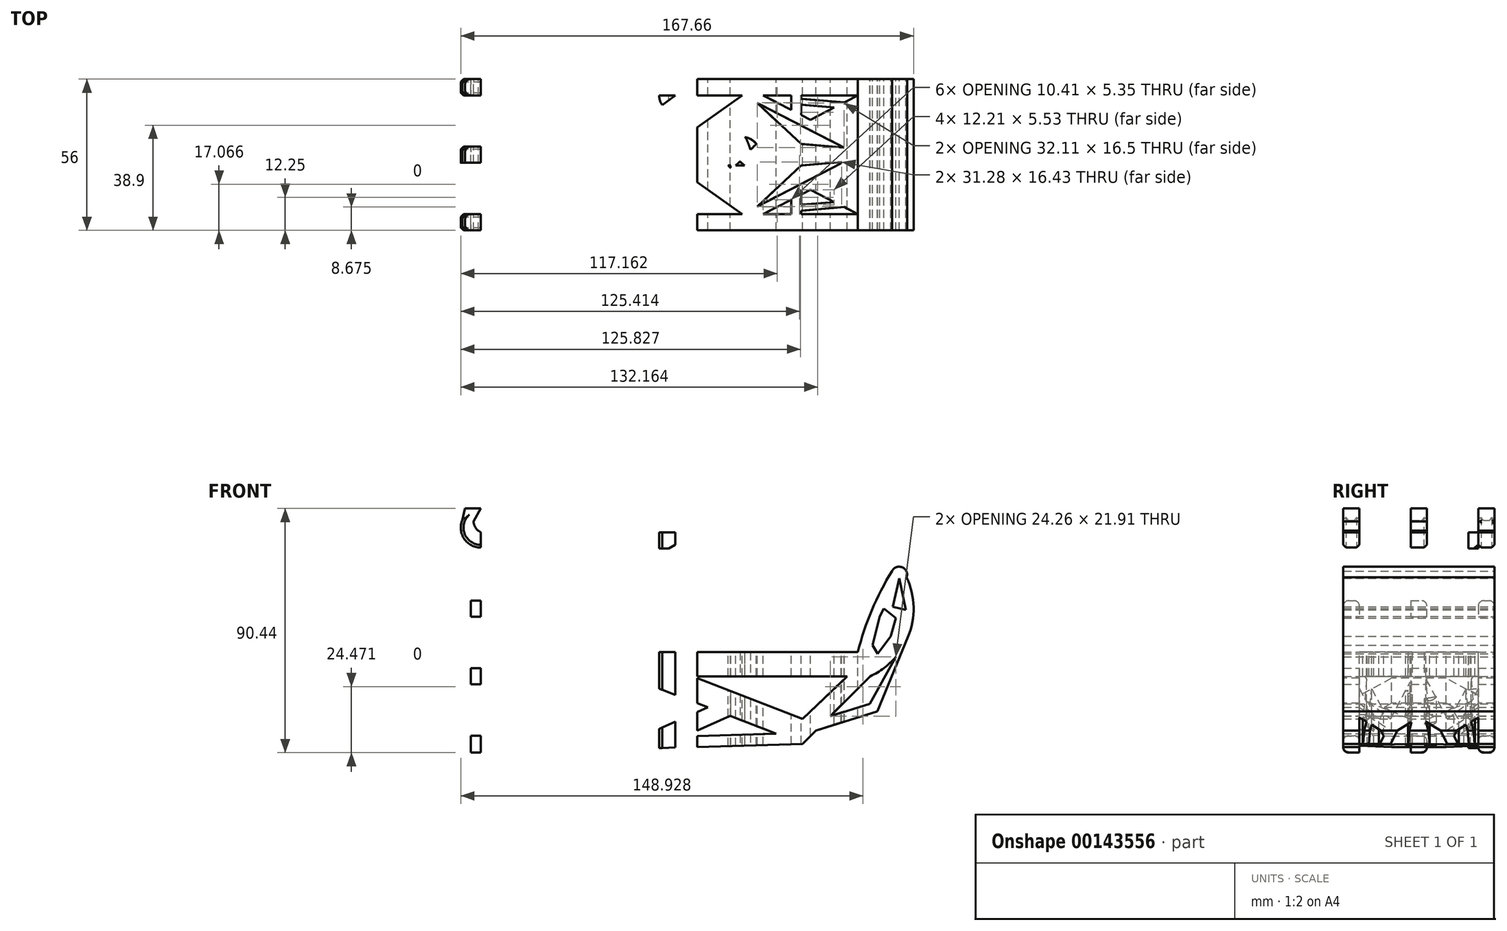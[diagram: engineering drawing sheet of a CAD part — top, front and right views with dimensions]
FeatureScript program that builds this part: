
annotation { "Feature Type Name" : "Feature", "Feature Type Description" : "" }
export const myFeature = defineFeature(function(context is Context, id is Id, definition is map)
    precondition{}
    {
        {
            var Q0;
            Q0=qCreatedBy(makeId("Front.planeOp"),FACE);
            var sketch = newSketch(context, id + "F0", { "sketchPlane" : qUnion([Q0])});
            skLineSegment(sketch, "E0.bottom", {"start": v(0, 0) * mm, "end": v(2.2, 0) * mm});
            skLineSegment(sketch, "E0.top", {"start": v(0, 6) * mm, "end": v(2.2, 6) * mm});
            skLineSegment(sketch, "E0.left", {"start": v(0, 0) * mm, "end": v(0, 6) * mm});
            skLineSegment(sketch, "E1.bottom", {"start": v(0, 6) * mm, "end": v(-4.66, 6) * mm});
            skLineSegment(sketch, "E1.top", {"start": v(0, 0.4) * mm, "end": v(-4.66, 0.4) * mm});
            skLineSegment(sketch, "E1.left", {"start": v(0, 6) * mm, "end": v(0, 0.4) * mm});
            skLineSegment(sketch, "E1.right", {"start": v(-4.66, 6) * mm, "end": v(-4.66, 0.4) * mm});
            skArc(sketch, "E2", {"start": v(-7.33, 10.05) * mm, "mid": v(-6.52, 7.68) * mm, "end": v(-4.66, 6) * mm});
            skArc(sketch, "E3", {"start": v(-11.52, 10.48) * mm, "mid": v(-10.76, 3.63) * mm, "end": v(-4.66, 0.4) * mm});
            skLineSegment(sketch, "E4", {"start": v(-4.66, 14.86) * mm, "end": v(-10.43, 14.86) * mm});
            skLineSegment(sketch, "E5", {"start": v(-10.43, 14.86) * mm, "end": v(-12, 8.6) * mm});
            skLineSegment(sketch, "E6", {"start": v(-4.66, 14.86) * mm, "end": v(-7.33, 10.05) * mm});
            skLineSegment(sketch, "E7", {"start": v(-8.25, 8.4) * mm, "end": v(-4.66, 6) * mm});
            skLineSegment(sketch, "E8.bottom", {"start": v(0, 6) * mm, "end": v(8, 6) * mm});
            skLineSegment(sketch, "E8.left", {"start": v(0, 6) * mm, "end": v(0, -7.26) * mm});
            skLineSegment(sketch, "E8.right", {"start": v(8, 6) * mm, "end": v(8, -7.26) * mm});
            skPoint(sketch, "E9.startSnap0", {"position": v(8, -0.63) * mm});
            skLineSegment(sketch, "E10.left", {"start": v(0, -7.26) * mm, "end": v(0, -22.3) * mm});
            skLineSegment(sketch, "E11", {"start": v(0, 3.2) * mm, "end": v(0, -22.3) * mm, "construction": true});
            skLineSegment(sketch, "E12.bottom", {"start": v(-8.37, -19.3) * mm, "end": v(0, -19.3) * mm});
            skLineSegment(sketch, "E12.top", {"start": v(-8.37, -25.3) * mm, "end": v(8, -25.3) * mm});
            skLineSegment(sketch, "E12.left", {"start": v(-8.37, -19.3) * mm, "end": v(-8.37, -25.3) * mm});
            skPoint(sketch, "E12.middle", {"position": v(0, -22.3) * mm});
            skLineSegment(sketch, "E13", {"start": v(8, -7.26) * mm, "end": v(8, -25.3) * mm});
            skLineSegment(sketch, "E14", {"start": v(0, -25.3) * mm, "end": v(-8.37, -25.3) * mm});
            skPoint(sketch, "E12.right.start.orphan", {"position": v(8.37, -19.3) * mm});
            skPoint(sketch, "E15.orphan", {"position": v(8.37, -25.3) * mm});
            skPoint(sketch, "E9.start.orphan", {"position": v(8, 0) * mm});
            skPoint(sketch, "E16.start.orphan", {"position": v(37.05, 0) * mm});
            skLineSegment(sketch, "E17.top", {"start": v(0, -47.3) * mm, "end": v(0.27, -47.3) * mm});
            skLineSegment(sketch, "E17.left", {"start": v(0, -22.3) * mm, "end": v(0, -38.12) * mm});
            skLineSegment(sketch, "E17.right", {"start": v(8, -22.3) * mm, "end": v(8, -38.33) * mm});
            skLineSegment(sketch, "E18.bottom", {"start": v(-8.37, -44.3) * mm, "end": v(0.18, -44.3) * mm});
            skLineSegment(sketch, "E18.top", {"start": v(-8.37, -50.3) * mm, "end": v(0.36, -50.3) * mm});
            skLineSegment(sketch, "E18.left", {"start": v(-8.37, -44.3) * mm, "end": v(-8.37, -50.3) * mm});
            skLineSegment(sketch, "E18.right", {"start": v(8.37, -47.3) * mm, "end": v(8.37, -47.46) * mm});
            skPoint(sketch, "E18.middle", {"position": v(0, -47.3) * mm});
            skLineSegment(sketch, "E19.bottom", {"start": v(8.37, -44.3) * mm, "end": v(8, -44.3) * mm});
            skLineSegment(sketch, "E19.top", {"start": v(0.36, -50.3) * mm, "end": v(-8.37, -50.3) * mm});
            skPoint(sketch, "E19.middle", {"position": v(8, -47.3) * mm});
            skPoint(sketch, "E19.right.end.orphan", {"position": v(-128, -50.3) * mm});
            skPoint(sketch, "E19.right.start.orphan", {"position": v(-119, -44.3) * mm});
            skLineSegment(sketch, "E20.bottom", {"start": v(0, 6) * mm, "end": v(75.48, 6) * mm});
            skLineSegment(sketch, "E20.left", {"start": v(0, 6) * mm, "end": v(0, 0) * mm});
            skLineSegment(sketch, "E21.bottom", {"start": v(8, -38.33) * mm, "end": v(133.63, -38.33) * mm});
            skLineSegment(sketch, "E21.left", {"start": v(8, -36.1) * mm, "end": v(8, -38.33) * mm});
            skLineSegment(sketch, "E22.bottom", {"start": v(8, -38.33) * mm, "end": v(135, -38.33) * mm});
            skLineSegment(sketch, "E22.top", {"start": v(8, -47.3) * mm, "end": v(8.37, -47.3) * mm});
            skPoint(sketch, "E23.endSnap0", {"position": v(4, -47.3) * mm});
            skLineSegment(sketch, "E24", {"start": v(4, -47.3) * mm, "end": v(4, -50.3) * mm});
            skLineSegment(sketch, "E25", {"start": v(139.5, -47.3) * mm, "end": v(114.54, -72.3) * mm});
            skLineSegment(sketch, "E26", {"start": v(104.76, -68.54) * mm, "end": v(87.68, -61.97) * mm});
            skLineSegment(sketch, "E27", {"start": v(131.03, -47.3) * mm, "end": v(114.54, -63.04) * mm});
            skLineSegment(sketch, "E28", {"start": v(114.54, -63.04) * mm, "end": v(73.6, -47.3) * mm});
            skPoint(sketch, "E29.centerSnap0", {"position": v(4, -59.8) * mm});
            skLineSegment(sketch, "E30", {"start": v(17.34, -47.3) * mm, "end": v(10.24, -53.9) * mm});
            skLineSegment(sketch, "E31", {"start": v(10.24, -53.9) * mm, "end": v(10.24, -64.47) * mm});
            skLineSegment(sketch, "E32", {"start": v(10.24, -64.47) * mm, "end": v(15, -66.9) * mm});
            skLineSegment(sketch, "E33", {"start": v(15, -66.9) * mm, "end": v(27.64, -60.68) * mm});
            skLineSegment(sketch, "E34.bottom", {"start": v(-4.5, -69.3) * mm, "end": v(4, -69.3) * mm});
            skLineSegment(sketch, "E34.top", {"start": v(-4.5, -75.3) * mm, "end": v(12.5, -75.3) * mm});
            skPoint(sketch, "E34.middle", {"position": v(4, -72.3) * mm});
            skLineSegment(sketch, "E35", {"start": v(21.25, -71) * mm, "end": v(36.6, -63.46) * mm});
            skLineSegment(sketch, "E36", {"start": v(12.5, -75.3) * mm, "end": v(114.54, -72.3) * mm});
            skPoint(sketch, "E37.end.orphan", {"position": v(4, -77.18) * mm});
            skLineSegment(sketch, "E38", {"start": v(21.25, -71) * mm, "end": v(52.02, -70.1) * mm});
            skPoint(sketch, "E39.orphan", {"position": v(135, -50.3) * mm});
            skPoint(sketch, "E19.left.start.orphan", {"position": v(144, -44.3) * mm});
            skLineSegment(sketch, "E40.trimOffspring", {"start": v(73.6, -47.3) * mm, "end": v(131.03, -47.3) * mm});
            skLineSegment(sketch, "E41", {"start": v(51.94, -55.92) * mm, "end": v(60.4, -51.48) * mm});
            skLineSegment(sketch, "E42", {"start": v(52.53, -48.45) * mm, "end": v(21.76, -47.45) * mm});
            skLineSegment(sketch, "E43", {"start": v(8.37, -47.46) * mm, "end": v(8, -47.3) * mm});
            skLineSegment(sketch, "E44", {"start": v(36.6, -63.46) * mm, "end": v(52.02, -70.1) * mm});
            skLineSegment(sketch, "E45", {"start": v(70.6, -69.54) * mm, "end": v(87.68, -61.97) * mm});
            skLineSegment(sketch, "E46", {"start": v(79.42, -58.8) * mm, "end": v(60.4, -67.23) * mm});
            skLineSegment(sketch, "E47", {"start": v(60.4, -67.23) * mm, "end": v(43.62, -60) * mm});
            skLineSegment(sketch, "E48.trimOffspring", {"start": v(43.62, -60) * mm, "end": v(51.94, -55.92) * mm});
            skPoint(sketch, "E49.end.orphan", {"position": v(60.4, -69.84) * mm});
            skPoint(sketch, "E49.start.orphan", {"position": v(82.58, -60.01) * mm});
            skLineSegment(sketch, "E50.trimOffspring", {"start": v(70.6, -69.54) * mm, "end": v(104.76, -68.54) * mm});
            skPoint(sketch, "E29.center.orphan", {"position": v(17.34, -59.8) * mm});
            skPoint(sketch, "E51.start.orphan", {"position": v(13.8, -50.6) * mm});
            skLineSegment(sketch, "E52", {"start": v(17.34, -47.3) * mm, "end": v(27.64, -60.68) * mm});
            skLineSegment(sketch, "E53", {"start": v(36.48, -56.34) * mm, "end": v(40.82, -54.2) * mm});
            skLineSegment(sketch, "E54", {"start": v(21.76, -47.45) * mm, "end": v(36.48, -56.34) * mm});
            skLineSegment(sketch, "E55.trimOffspring", {"start": v(36.48, -56.34) * mm, "end": v(52.53, -48.45) * mm});
            skArc(sketch, "E56", {"start": v(147.62, -8.33) * mm, "mid": v(140.11, -22.82) * mm, "end": v(135, -38.33) * mm});
            skArc(sketch, "E57", {"start": v(139.5, -47.3) * mm, "mid": v(144.65, -44.25) * mm, "end": v(149.02, -40.15) * mm});
            skArc(sketch, "E58", {"start": v(153.03, -10.64) * mm, "mid": v(151.41, -6.95) * mm, "end": v(147.62, -8.33) * mm});
            skLineSegment(sketch, "E59", {"start": v(150.25, -11.01) * mm, "end": v(152.71, -22.66) * mm});
            skLineSegment(sketch, "E60", {"start": v(147.92, -21.6) * mm, "end": v(152.71, -22.66) * mm});
            skLineSegment(sketch, "E61.trimOffspring", {"start": v(147.92, -21.6) * mm, "end": v(150.25, -11.01) * mm});
            skLineSegment(sketch, "E62", {"start": v(149.02, -40.15) * mm, "end": v(139.32, -57.51) * mm});
            skLineSegment(sketch, "E63", {"start": v(139.32, -57.51) * mm, "end": v(124.76, -62.06) * mm});
            skLineSegment(sketch, "E64", {"start": v(124.76, -62.06) * mm, "end": v(119.44, -67.4) * mm});
            skLineSegment(sketch, "E65", {"start": v(119.44, -67.4) * mm, "end": v(142.16, -60.29) * mm});
            skLineSegment(sketch, "E66", {"start": v(142.16, -60.29) * mm, "end": v(153.54, -32.79) * mm});
            skArc(sketch, "E67.trimOffspring", {"start": v(153.54, -32.79) * mm, "mid": v(155.61, -21.66) * mm, "end": v(153.03, -10.64) * mm});
            skLineSegment(sketch, "E68", {"start": v(143.06, -25.11) * mm, "end": v(140.34, -35.8) * mm});
            skLineSegment(sketch, "E69", {"start": v(140.34, -35.8) * mm, "end": v(142.29, -38.91) * mm});
            skLineSegment(sketch, "E70", {"start": v(142.29, -38.91) * mm, "end": v(147.14, -32.5) * mm});
            skLineSegment(sketch, "E71", {"start": v(147.14, -32.5) * mm, "end": v(149.09, -25.7) * mm});
            skLineSegment(sketch, "E72", {"start": v(149.09, -25.7) * mm, "end": v(144.62, -22.2) * mm});
            skLineSegment(sketch, "E73", {"start": v(144.62, -22.2) * mm, "end": v(143.06, -25.11) * mm});
            skPoint(sketch, "E20.right.end.orphan", {"position": v(129.94, 0) * mm});
            skLineSegment(sketch, "E74.trimOffspring", {"start": v(79.42, -58.8) * mm, "end": v(60.4, -51.48) * mm});
            skPoint(sketch, "E34.right.start.orphan", {"position": v(12.5, -69.3) * mm});
            skLineSegment(sketch, "E75", {"start": v(0, -38.12) * mm, "end": v(0.18, -44.3) * mm});
            skLineSegment(sketch, "E76", {"start": v(1.1, -75.3) * mm, "end": v(-8.37, -75.58) * mm});
            skLineSegment(sketch, "E77", {"start": v(-8.37, -75.58) * mm, "end": v(-8.37, -69.3) * mm});
            skLineSegment(sketch, "E78", {"start": v(-8.37, -69.3) * mm, "end": v(-4.5, -69.3) * mm});
            skPoint(sketch, "E79.trimOffspring.start.orphan", {"position": v(-4.5, -72.3) * mm});
            skLineSegment(sketch, "E80.trimOffspring", {"start": v(4, -69.3) * mm, "end": v(4, -72.3) * mm});
            skLineSegment(sketch, "E81.trimOffspring", {"start": v(0.18, -44.3) * mm, "end": v(-8.37, -44.3) * mm});
            skPoint(sketch, "E82.orphan", {"position": v(8.37, -50.3) * mm});
            skLineSegment(sketch, "E83.trimOffspring", {"start": v(0.36, -50.3) * mm, "end": v(0.92, -69.3) * mm});
            skLineSegment(sketch, "E84.trimOffspring", {"start": v(8, 0) * mm, "end": v(64.97, 0) * mm});
            skPoint(sketch, "E85.orphan", {"position": v(8, -19.3) * mm});
            skLineSegment(sketch, "E86", {"start": v(75.48, 6) * mm, "end": v(64.97, 0) * mm});
            skSolve(sketch);
        }
        {
            var Q0;
            Q0=qSketchRegion(id+"F0",true);
            extrude(context, id + "F1", {"entities" : qUnion([Q0]), "depth" : 5.5 * mm});
        }
        {
            var Q0;
            Q0=makeQuery(id+"F1.opExtrude","CAP_EDGE",EDGE,{"disambiguationData":[OSD([sQuery(id+"F0.wireOp",EDGE,"E12.bottom")])],"isStart":false});
            var Q1;
            Q1=makeQuery(id+"F1.opExtrude","CAP_EDGE",EDGE,{"disambiguationData":[OSD([sQuery(id+"F0.wireOp",EDGE,"E12.bottom")])],"isStart":true});
            var Q2;
            Q2=makeQuery(id+"F1.opExtrude","CAP_EDGE",EDGE,{"disambiguationData":[OSD([sQuery(id+"F0.wireOp",EDGE,"E14")])],"isStart":true});
            var Q3;
            Q3=makeQuery(id+"F1.opExtrude","CAP_EDGE",EDGE,{"disambiguationData":[OSD([sQuery(id+"F0.wireOp",EDGE,"E14")])],"isStart":false});
            fillet(context, id + "F2", {"entities" : qUnion([Q0, Q1, Q2, Q3]), "radius" : 2.66 * mm, "tangentPropagation" : true, "allowEdgeOverflow" : false});
        }
        {
            var Q0;
            Q0=makeQuery(id+"F1.opExtrude","SWEPT_EDGE",EDGE,{"disambiguationData":[OSD([sQuery(id+"F0.wireOp",EDGE,"E2"),sQuery(id+"F0.wireOp",EDGE,"E4"),sQuery(id+"F0.wireOp",EDGE,"E6")])]});
            fillet(context, id + "F3", {"entities" : qUnion([Q0]), "radius" : 1.62 * mm, "tangentPropagation" : true, "allowEdgeOverflow" : false});
        }
        {
            var Q0;
            Q0=makeQuery(id+"F1.opExtrude","CAP_EDGE",EDGE,{"disambiguationData":[OSD([sQuery(id+"F0.wireOp",EDGE,"E2")])],"isStart":true});
            var Q1;
            Q1=makeQuery(id+"F1.opExtrude","CAP_EDGE",EDGE,{"disambiguationData":[OSD([sQuery(id+"F0.wireOp",EDGE,"E2")])],"isStart":false});
            var Q2;
            Q2=makeQuery(id+"F1.opExtrude","CAP_EDGE",EDGE,{"disambiguationData":[OSD([sQuery(id+"F0.wireOp",EDGE,"E6")])],"isStart":false});
            var Q3;
            Q3=makeQuery(id+"F1.opExtrude","CAP_EDGE",EDGE,{"disambiguationData":[OSD([sQuery(id+"F0.wireOp",EDGE,"E6")])],"isStart":true});
            fillet(context, id + "F4", {"entities" : qUnion([Q0, Q1, Q2, Q3]), "radius" : .6 * mm, "tangentPropagation" : true, "allowEdgeOverflow" : false});
        }
        {
            var Q0;
            Q0=makeQuery(id+"F1.opExtrude","CAP_EDGE",EDGE,{"disambiguationData":[OSD([sQuery(id+"F0.wireOp",EDGE,"E3")])],"isStart":true});
            var Q1;
            Q1=makeQuery(id+"F1.opExtrude","CAP_EDGE",EDGE,{"disambiguationData":[OSD([sQuery(id+"F0.wireOp",EDGE,"E5")])],"isStart":true});
            var Q2;
            Q2=makeQuery(id+"F1.opExtrude","CAP_EDGE",EDGE,{"disambiguationData":[OSD([sQuery(id+"F0.wireOp",EDGE,"E1.top")])],"isStart":false});
            var Q3;
            Q3=makeQuery(id+"F1.opExtrude","CAP_EDGE",EDGE,{"disambiguationData":[OSD([sQuery(id+"F0.wireOp",EDGE,"E3")])],"isStart":false});
            var Q4;
            Q4=makeQuery(id+"F1.opExtrude","CAP_EDGE",EDGE,{"disambiguationData":[OSD([sQuery(id+"F0.wireOp",EDGE,"E5")])],"isStart":false});
            var Q5;
            Q5=makeQuery(id+"F1.opExtrude","CAP_EDGE",EDGE,{"disambiguationData":[OSD([sQuery(id+"F0.wireOp",EDGE,"E1.top")])],"isStart":true});
            fillet(context, id + "F5", {"entities" : qUnion([Q0, Q1, Q2, Q3, Q4, Q5]), "radius" : 1.49 * mm, "tangentPropagation" : true, "allowEdgeOverflow" : false});
        }
        {
            var Q0;
            Q0=qSketchRegion(id+"F0",true);
            extrude(context, id + "F6", {"entities" : qUnion([Q0]), "operationType" : NewBodyOperationType.ADD, "depth" : 56 * mm});
        }
        {
            var Q0;
            {var subQ0=sQuery(id+"F0.wireOp",EDGE,"E76");Q0=makeQuery(id+"F6.boolean.opBoolean","MERGE",FACE,{"derivedFrom":[makeQuery(id+"F1.opExtrude","SWEPT_FACE",FACE,{"disambiguationData":[OSD([subQ0])]}),makeQuery(id+"F6.opExtrude","SWEPT_FACE",FACE,{"disambiguationData":[OSD([subQ0])]})]});}
            var sketch = newSketch(context, id + "F7", { "sketchPlane" : qUnion([Q0])});
            skLineSegment(sketch, "E87.bottom", {"start": v(-1.12, 56) * mm, "end": v(-15.4, 56) * mm});
            skLineSegment(sketch, "E87.top", {"start": v(-1.12, 0) * mm, "end": v(-15.4, 0) * mm});
            skLineSegment(sketch, "E87.left", {"start": v(-1.12, 56) * mm, "end": v(-1.12, 0) * mm});
            skLineSegment(sketch, "E87.right", {"start": v(-15.4, 56) * mm, "end": v(-15.4, 0) * mm});
            skLineSegment(sketch, "E88.top", {"start": v(-1.12, 50) * mm, "end": v(-15.4, 50) * mm});
            skLineSegment(sketch, "E88.right", {"start": v(-15.4, 56) * mm, "end": v(-15.4, 50) * mm});
            skLineSegment(sketch, "E89.top", {"start": v(-1.12, 6) * mm, "end": v(-15.4, 6) * mm});
            skLineSegment(sketch, "E89.right", {"start": v(-15.4, 0) * mm, "end": v(-15.4, 6) * mm});
            skLineSegment(sketch, "E90.top", {"start": v(-1.12, 31) * mm, "end": v(-15.4, 31) * mm});
            skLineSegment(sketch, "E90.left", {"start": v(-1.12, 28) * mm, "end": v(-1.12, 31) * mm});
            skLineSegment(sketch, "E90.right", {"start": v(-15.4, 28) * mm, "end": v(-15.4, 31) * mm});
            skLineSegment(sketch, "E91.bottom", {"start": v(-15.4, 31) * mm, "end": v(-1.12, 31) * mm});
            skLineSegment(sketch, "E91.top", {"start": v(-15.4, 25) * mm, "end": v(-1.12, 25) * mm});
            skLineSegment(sketch, "E91.left", {"start": v(-15.4, 31) * mm, "end": v(-15.4, 25) * mm});
            skSolve(sketch);
        }
        {
            var Q0;
            {var subQ0=sQuery(id+"F7.wireOp",EDGE,"E88.top");var subQ1=sQuery(id+"F7.wireOp",EDGE,"E87.left");var subQ2=makeQuery(id+"F7.imprint","INTERSECT",VERTEX,{"derivedFrom":[subQ1,subQ0]});Q0=makeQuery(id+"F7.imprint","IMPRINT",FACE,{"disambiguationData":[TD([[makeQuery(id+"F7.imprint","IMPRINT",EDGE,{"disambiguationData":[TD([[subQ2,-1.0]])],"derivedFrom":subQ1}),-1.0]])]});}
            var Q1;
            {var subQ0=sQuery(id+"F7.wireOp",EDGE,"E88.top");var subQ1=sQuery(id+"F7.wireOp",EDGE,"E87.right");var subQ2=makeQuery(id+"F7.imprint","INTERSECT",VERTEX,{"derivedFrom":[subQ1,subQ0,sQuery(id+"F7.wireOp",EDGE,"E88.right")]});Q1=makeQuery(id+"F7.imprint","IMPRINT",FACE,{"disambiguationData":[TD([[makeQuery(id+"F7.imprint","IMPRINT",EDGE,{"disambiguationData":[TD([[subQ2,-1.0]])],"derivedFrom":subQ1}),1.0]])]});}
            var Q2;
            {var subQ0=sQuery(id+"F7.wireOp",EDGE,"E89.top");var subQ1=sQuery(id+"F7.wireOp",EDGE,"E87.left");var subQ2=makeQuery(id+"F7.imprint","INTERSECT",VERTEX,{"derivedFrom":[subQ1,subQ0]});Q2=makeQuery(id+"F7.imprint","IMPRINT",FACE,{"disambiguationData":[TD([[makeQuery(id+"F7.imprint","IMPRINT",EDGE,{"disambiguationData":[TD([[subQ2,1.0]])],"derivedFrom":subQ1}),-1.0]])]});}
            var Q3;
            {var subQ0=sQuery(id+"F7.wireOp",EDGE,"E89.top");var subQ1=sQuery(id+"F7.wireOp",EDGE,"E87.right");var subQ2=makeQuery(id+"F7.imprint","INTERSECT",VERTEX,{"derivedFrom":[subQ1,subQ0,sQuery(id+"F7.wireOp",EDGE,"E89.right")]});Q3=makeQuery(id+"F7.imprint","IMPRINT",FACE,{"disambiguationData":[TD([[makeQuery(id+"F7.imprint","IMPRINT",EDGE,{"disambiguationData":[TD([[subQ2,1.0]])],"derivedFrom":subQ1}),1.0]])]});}
            extrude(context, id + "F8", {"entities" : qUnion([Q0, Q1, Q2, Q3]), "operationType" : NewBodyOperationType.REMOVE, "endBound" : BoundingType.THROUGH_ALL, "oppositeDirection" : true, "depth" : 25 * mm});
        }
        {
            var Q0;
            {var subQ0=sQuery(id+"F0.wireOp",EDGE,"E20.bottom");var subQ1=sQuery(id+"F0.wireOp",EDGE,"E1.bottom");Q0=makeQuery(id+"F6.boolean.opBoolean","MERGE",FACE,{"derivedFrom":[makeQuery(id+"F1.opExtrude","SWEPT_FACE",FACE,{"disambiguationData":[OSD([subQ1,subQ0])]}),makeQuery(id+"F6.opExtrude","SWEPT_FACE",FACE,{"disambiguationData":[OSD([subQ1,subQ0])]})]});}
            var sketch = newSketch(context, id + "F9", { "sketchPlane" : qUnion([Q0])});
            skLineSegment(sketch, "E92.top", {"start": v(15.03, -50) * mm, "end": v(39.96, -50) * mm});
            skLineSegment(sketch, "E93", {"start": v(12.55, -9.31) * mm, "end": v(7.82, -15.65) * mm});
            skLineSegment(sketch, "E94", {"start": v(7.82, -15.65) * mm, "end": v(15.03, -24.07) * mm});
            skPoint(sketch, "E94.endSnap0", {"position": v(7.82, -28) * mm});
            skLineSegment(sketch, "E95", {"start": v(15.03, -31.97) * mm, "end": v(7.82, -40.5) * mm});
            skPoint(sketch, "E95.endSnap0", {"position": v(-1.3, -40.5) * mm});
            skLineSegment(sketch, "E96", {"start": v(7.82, -40.5) * mm, "end": v(12.53, -46.7) * mm});
            skPoint(sketch, "E97.orphan", {"position": v(7.82, -6) * mm});
            skPoint(sketch, "E98.orphan", {"position": v(7.82, -50) * mm});
            skLineSegment(sketch, "E99", {"start": v(15.03, -6) * mm, "end": v(40.59, -6) * mm});
            skLineSegment(sketch, "E100", {"start": v(69.45, -6) * mm, "end": v(66.07, -12.15) * mm});
            skPoint(sketch, "E100.endSnap0", {"position": v(15.03, -15.04) * mm});
            skLineSegment(sketch, "E101", {"start": v(64.61, -15.53) * mm, "end": v(66.79, -24.07) * mm});
            skLineSegment(sketch, "E102", {"start": v(66.74, -31.97) * mm, "end": v(64.49, -40.5) * mm});
            skLineSegment(sketch, "E103", {"start": v(40.86, -6.91) * mm, "end": v(27.3, -15.92) * mm});
            skLineSegment(sketch, "E104", {"start": v(43.56, -6.98) * mm, "end": v(54.86, -15.3) * mm});
            skLineSegment(sketch, "E105", {"start": v(40.21, -49.18) * mm, "end": v(27.11, -40.23) * mm});
            skLineSegment(sketch, "E106", {"start": v(42.59, -49.16) * mm, "end": v(54.67, -40.56) * mm});
            skPoint(sketch, "E92.right.start.orphan", {"position": v(67.79, -6) * mm});
            skLineSegment(sketch, "E107", {"start": v(69.45, -50) * mm, "end": v(66.22, -43.81) * mm});
            skLineSegment(sketch, "E108", {"start": v(18.38, -28) * mm, "end": v(28.6, -21.22) * mm});
            skLineSegment(sketch, "E109", {"start": v(42.24, -12.16) * mm, "end": v(50.7, -18.38) * mm});
            skLineSegment(sketch, "E110", {"start": v(63.76, -28) * mm, "end": v(52.31, -36.15) * mm});
            skLineSegment(sketch, "E111", {"start": v(41.4, -43.9) * mm, "end": v(31.25, -36.89) * mm});
            skLineSegment(sketch, "E112", {"start": v(15.03, -6) * mm, "end": v(27.3, -15.92) * mm});
            skLineSegment(sketch, "E113", {"start": v(69.45, -6) * mm, "end": v(63.55, -10.77) * mm});
            skLineSegment(sketch, "E114.right", {"start": v(45.24, -25) * mm, "end": v(45.24, -25.57) * mm});
            skPoint(sketch, "E114.middle", {"position": v(42.24, -28) * mm});
            skLineSegment(sketch, "E115.trimOffspring", {"start": v(31.48, -19.3) * mm, "end": v(38.63, -25.09) * mm});
            skLineSegment(sketch, "E116.trimOffspring", {"start": v(52.5, -19.7) * mm, "end": v(43.24, -27.2) * mm});
            skLineSegment(sketch, "E117", {"start": v(12.55, -9.31) * mm, "end": v(24.22, -17.97) * mm});
            skLineSegment(sketch, "E118", {"start": v(75.48, -56) * mm, "end": v(0, -56) * mm});
            skLineSegment(sketch, "E119", {"start": v(12.53, -46.7) * mm, "end": v(24.06, -38.15) * mm});
            skLineSegment(sketch, "E120.trimOffspring", {"start": v(28.6, -21.22) * mm, "end": v(36.9, -27.37) * mm});
            skLineSegment(sketch, "E121.trimOffspring", {"start": v(28.4, -34.92) * mm, "end": v(36.9, -28.63) * mm});
            skLineSegment(sketch, "E122", {"start": v(15.03, -50) * mm, "end": v(27.11, -40.23) * mm});
            skLineSegment(sketch, "E123.trimOffspring", {"start": v(45.24, -30.43) * mm, "end": v(52.31, -36.15) * mm});
            skLineSegment(sketch, "E124.trimOffspring", {"start": v(41.61, -25.13) * mm, "end": v(50.7, -18.38) * mm});
            skLineSegment(sketch, "E125.trimOffspring", {"start": v(41.61, -30.87) * mm, "end": v(50.48, -37.45) * mm});
            skPoint(sketch, "E126.orphan", {"position": v(39.24, -28) * mm});
            skLineSegment(sketch, "E127.trimOffspring", {"start": v(43.24, -28.8) * mm, "end": v(52.31, -36.15) * mm});
            skLineSegment(sketch, "E128.trimOffspring", {"start": v(43.24, -27.2) * mm, "end": v(52.5, -19.7) * mm});
            skLineSegment(sketch, "E129.trimOffspring", {"start": v(52.5, -19.7) * mm, "end": v(63.76, -28) * mm});
            skLineSegment(sketch, "E130.trimOffspring", {"start": v(56.48, -16.48) * mm, "end": v(66.79, -24.07) * mm});
            skLineSegment(sketch, "E131.trimOffspring", {"start": v(56.32, -39.39) * mm, "end": v(60.64, -42.88) * mm});
            skLineSegment(sketch, "E132.trimOffspring", {"start": v(54.67, -40.56) * mm, "end": v(59.55, -44.18) * mm});
            skLineSegment(sketch, "E133.trimOffspring", {"start": v(31.25, -36.89) * mm, "end": v(38.63, -30.91) * mm});
            skLineSegment(sketch, "E134.trimOffspring", {"start": v(31.48, -19.3) * mm, "end": v(39.24, -25.57) * mm});
            skPoint(sketch, "E135.end.orphan", {"position": v(45.24, -28) * mm});
            skLineSegment(sketch, "E136.trimOffspring", {"start": v(45.24, -30.43) * mm, "end": v(45.24, -31) * mm});
            skLineSegment(sketch, "E137.trimOffspring", {"start": v(56.32, -39.39) * mm, "end": v(66.74, -31.97) * mm});
            skLineSegment(sketch, "E138.trimOffspring", {"start": v(50.48, -37.45) * mm, "end": v(41.4, -43.9) * mm});
            skLineSegment(sketch, "E139.trimOffspring", {"start": v(31.48, -19.3) * mm, "end": v(42.24, -12.16) * mm});
            skLineSegment(sketch, "E140.trimOffspring", {"start": v(24.22, -17.97) * mm, "end": v(15.03, -24.07) * mm});
            skLineSegment(sketch, "E141.trimOffspring", {"start": v(54.86, -15.3) * mm, "end": v(59.55, -11.82) * mm});
            skLineSegment(sketch, "E142.trimOffspring", {"start": v(56.48, -16.48) * mm, "end": v(60.64, -13.12) * mm});
            skPoint(sketch, "E143.orphan", {"position": v(67.79, -50) * mm});
            skPoint(sketch, "E144.orphan", {"position": v(67.79, -28) * mm});
            skArc(sketch, "E145", {"start": v(42.86, -50) * mm, "mid": v(42.79, -49.56) * mm, "end": v(42.59, -49.16) * mm});
            skArc(sketch, "E146", {"start": v(40.59, -6) * mm, "mid": v(40.66, -6.48) * mm, "end": v(40.86, -6.91) * mm});
            skPoint(sketch, "E147.trimOffspring.end.orphan", {"position": v(39.24, -31) * mm});
            skLineSegment(sketch, "E148.trimOffspring", {"start": v(38.63, -30.91) * mm, "end": v(31.25, -36.89) * mm});
            skArc(sketch, "E149", {"start": v(36.9, -27.37) * mm, "mid": v(36.83, -28) * mm, "end": v(36.9, -28.63) * mm});
            skLineSegment(sketch, "E150.trimOffspring", {"start": v(43.89, -6) * mm, "end": v(57.7, -6) * mm});
            skArc(sketch, "E151.trimOffspring", {"start": v(43.56, -6.98) * mm, "mid": v(43.8, -6.51) * mm, "end": v(43.89, -6) * mm});
            skArc(sketch, "E152.trimOffspring", {"start": v(40.21, -49.18) * mm, "mid": v(40.03, -49.57) * mm, "end": v(39.96, -50) * mm});
            skLineSegment(sketch, "E153.trimOffspring", {"start": v(42.86, -50) * mm, "end": v(67.4, -50) * mm});
            skArc(sketch, "E154.trimOffspring", {"start": v(38.63, -30.91) * mm, "mid": v(40.13, -31.25) * mm, "end": v(41.61, -30.87) * mm});
            skArc(sketch, "E155.trimOffspring", {"start": v(43.24, -28.8) * mm, "mid": v(43.34, -28) * mm, "end": v(43.24, -27.2) * mm});
            skPoint(sketch, "E156.orphan", {"position": v(40.08, -29.74) * mm});
            skArc(sketch, "E157.trimOffspring", {"start": v(41.61, -25.13) * mm, "mid": v(40.13, -24.75) * mm, "end": v(38.63, -25.09) * mm});
            skPoint(sketch, "E114.left.start.orphan", {"position": v(39.24, -25) * mm});
            skArc(sketch, "E158", {"start": v(64.5, -40.47) * mm, "mid": v(62.43, -41.45) * mm, "end": v(60.64, -42.88) * mm});
            skArc(sketch, "E159", {"start": v(66.22, -43.81) * mm, "mid": v(64.8, -44.36) * mm, "end": v(63.55, -45.23) * mm});
            skLineSegment(sketch, "E160", {"start": v(40.08, -28) * mm, "end": v(80.79, -28) * mm, "construction": true});
            skArc(sketch, "E161.trimOffspring", {"start": v(59.55, -44.18) * mm, "mid": v(58.18, -46.95) * mm, "end": v(57.7, -50) * mm});
            skLineSegment(sketch, "E162.trimOffspring", {"start": v(63.55, -45.23) * mm, "end": v(69.45, -50) * mm});
            skLineSegment(sketch, "E163.trimOffspring", {"start": v(62.52, -46.39) * mm, "end": v(67.4, -50) * mm});
            skArc(sketch, "E164.trimOffspring", {"start": v(62.52, -46.39) * mm, "mid": v(61.7, -48.11) * mm, "end": v(61.4, -50) * mm});
            skArc(sketch, "E165.MirrorCS", {"start": v(62.52, -9.61) * mm, "mid": v(61.7, -7.89) * mm, "end": v(61.4, -6) * mm});
            skArc(sketch, "E166.MirrorCS", {"start": v(59.55, -11.82) * mm, "mid": v(58.18, -9.05) * mm, "end": v(57.7, -6) * mm});
            skArc(sketch, "E167.MirrorCS", {"start": v(64.5, -15.53) * mm, "mid": v(62.43, -14.55) * mm, "end": v(60.64, -13.12) * mm});
            skArc(sketch, "E168.MirrorCS", {"start": v(66.22, -12.19) * mm, "mid": v(64.8, -11.64) * mm, "end": v(63.55, -10.77) * mm});
            skLineSegment(sketch, "E169.trimOffspring", {"start": v(24.06, -38.15) * mm, "end": v(15.03, -31.97) * mm});
            skLineSegment(sketch, "E170.trimOffspring", {"start": v(28.4, -34.92) * mm, "end": v(18.38, -28) * mm});
            skLineSegment(sketch, "E171.trimOffspring", {"start": v(62.52, -9.61) * mm, "end": v(67.4, -6) * mm});
            skLineSegment(sketch, "E172.trimOffspring", {"start": v(63.55, -10.77) * mm, "end": v(69.45, -6) * mm});
            skLineSegment(sketch, "E173.trimOffspring", {"start": v(60.64, -13.12) * mm, "end": v(56.48, -16.48) * mm});
            skLineSegment(sketch, "E174.trimOffspring", {"start": v(61.4, -6) * mm, "end": v(67.79, -6) * mm});
            skLineSegment(sketch, "E175", {"start": v(64.5, -15.53) * mm, "end": v(64.61, -15.53) * mm});
            skPoint(sketch, "E176.orphan", {"position": v(64.49, -15.04) * mm});
            skSolve(sketch);
        }
        {
            var Q0;
            Q0=makeQuery(id+"F9.imprint","IMPRINT",FACE,{"disambiguationData":[TD([[makeQuery(id+"F9.imprint","IMPRINT",EDGE,{"derivedFrom":sQuery(id+"F9.wireOp",EDGE,"E109")}),-1.0]])]});
            var Q1;
            Q1=makeQuery(id+"F9.imprint","IMPRINT",FACE,{"disambiguationData":[TD([[makeQuery(id+"F9.imprint","IMPRINT",EDGE,{"derivedFrom":sQuery(id+"F9.wireOp",EDGE,"E111")}),-1.0]])]});
            var Q2;
            Q2=makeQuery(id+"F9.imprint","IMPRINT",FACE,{"disambiguationData":[TD([[makeQuery(id+"F9.imprint","IMPRINT",EDGE,{"derivedFrom":sQuery(id+"F9.wireOp",EDGE,"E108")}),-1.0]])]});
            var Q3;
            Q3=makeQuery(id+"F9.imprint","IMPRINT",FACE,{"disambiguationData":[TD([[makeQuery(id+"F9.imprint","IMPRINT",EDGE,{"derivedFrom":sQuery(id+"F9.wireOp",EDGE,"E93")}),1.0]])]});
            var Q4;
            Q4=makeQuery(id+"F9.imprint","IMPRINT",FACE,{"disambiguationData":[TD([[makeQuery(id+"F9.imprint","IMPRINT",EDGE,{"derivedFrom":sQuery(id+"F9.wireOp",EDGE,"E99")}),-1.0]])]});
            var Q5;
            Q5=makeQuery(id+"F9.imprint","IMPRINT",FACE,{"disambiguationData":[TD([[makeQuery(id+"F9.imprint","IMPRINT",EDGE,{"derivedFrom":sQuery(id+"F9.wireOp",EDGE,"E104")}),1.0]])]});
            var Q6;
            {var subQ0=sQuery(id+"F9.wireOp",EDGE,"E165.MirrorCS");Q6=makeQuery(id+"F9.imprint","IMPRINT",FACE,{"disambiguationData":[TD([[makeQuery(id+"F9.imprint","IMPRINT",EDGE,{"derivedFrom":subQ0}),-1.0]])]});}
            var Q7;
            {var subQ0=sQuery(id+"F9.wireOp",EDGE,"E100");Q7=makeQuery(id+"F9.imprint","IMPRINT",FACE,{"disambiguationData":[TD([[makeQuery(id+"F9.imprint","IMPRINT",EDGE,{"derivedFrom":subQ0}),-1.0]])]});}
            var Q8;
            Q8=makeQuery(id+"F9.imprint","IMPRINT",FACE,{"disambiguationData":[TD([[makeQuery(id+"F9.imprint","IMPRINT",EDGE,{"derivedFrom":sQuery(id+"F9.wireOp",EDGE,"E101")}),-1.0]])]});
            var Q9;
            {var subQ4=sQuery(id+"F9.wireOp",EDGE,"E110");Q9=makeQuery(id+"F9.imprint","IMPRINT",FACE,{"disambiguationData":[TD([[makeQuery(id+"F9.imprint","IMPRINT",EDGE,{"derivedFrom":subQ4}),-1.0]])]});}
            var Q10;
            Q10=makeQuery(id+"F9.imprint","IMPRINT",FACE,{"disambiguationData":[TD([[makeQuery(id+"F9.imprint","IMPRINT",EDGE,{"derivedFrom":sQuery(id+"F9.wireOp",EDGE,"E131.trimOffspring")}),1.0]])]});
            var Q11;
            Q11=makeQuery(id+"F9.imprint","IMPRINT",FACE,{"disambiguationData":[TD([[makeQuery(id+"F9.imprint","IMPRINT",EDGE,{"derivedFrom":sQuery(id+"F9.wireOp",EDGE,"E107")}),1.0]])]});
            var Q12;
            {var subQ0=sQuery(id+"F9.wireOp",EDGE,"E163.trimOffspring");Q12=makeQuery(id+"F9.imprint","IMPRINT",FACE,{"disambiguationData":[TD([[makeQuery(id+"F9.imprint","IMPRINT",EDGE,{"derivedFrom":subQ0}),-1.0]])]});}
            var Q13;
            Q13=makeQuery(id+"F9.imprint","IMPRINT",FACE,{"disambiguationData":[TD([[makeQuery(id+"F9.imprint","IMPRINT",EDGE,{"derivedFrom":sQuery(id+"F9.wireOp",EDGE,"E106")}),-1.0]])]});
            var Q14;
            Q14=makeQuery(id+"F9.imprint","IMPRINT",FACE,{"disambiguationData":[TD([[makeQuery(id+"F9.imprint","IMPRINT",EDGE,{"derivedFrom":sQuery(id+"F9.wireOp",EDGE,"E92.top")}),1.0]])]});
            var Q15;
            Q15=makeQuery(id+"F9.imprint","IMPRINT",FACE,{"disambiguationData":[TD([[makeQuery(id+"F9.imprint","IMPRINT",EDGE,{"derivedFrom":sQuery(id+"F9.wireOp",EDGE,"E95")}),1.0]])]});
            extrude(context, id + "F10", {"entities" : qUnion([Q0, Q1, Q2, Q3, Q4, Q5, Q6, Q7, Q8, Q9, Q10, Q11, Q12, Q13, Q14, Q15]), "operationType" : NewBodyOperationType.REMOVE, "endBound" : BoundingType.THROUGH_ALL, "oppositeDirection" : true, "depth" : 25 * mm});
        }
        {
            var Q0;
            {var subQ0=sQuery(id+"F0.wireOp",EDGE,"E22.bottom");Q0=makeQuery(id+"F6.boolean.opBoolean","MERGE",FACE,{"derivedFrom":[makeQuery(id+"F1.opExtrude","SWEPT_FACE",FACE,{"disambiguationData":[OSD([subQ0])]}),makeQuery(id+"F6.opExtrude","SWEPT_FACE",FACE,{"disambiguationData":[OSD([subQ0])]})]});}
            var sketch = newSketch(context, id + "F11", { "sketchPlane" : qUnion([Q0])});
            skLineSegment(sketch, "E177.bottom", {"start": v(69.34, -31.97) * mm, "end": v(69.45, -31.97) * mm});
            skLineSegment(sketch, "E177.top", {"start": v(66.74, -24.03) * mm, "end": v(66.85, -24.03) * mm});
            skLineSegment(sketch, "E177.left", {"start": v(66.74, -30.12) * mm, "end": v(66.74, -25.88) * mm});
            skPoint(sketch, "E177.middle", {"position": v(135, -28) * mm});
            skLineSegment(sketch, "E178.bottom", {"start": v(72.46, -6) * mm, "end": v(92.19, -6) * mm});
            skLineSegment(sketch, "E178.top", {"start": v(72.46, -50) * mm, "end": v(92.19, -50) * mm});
            skLineSegment(sketch, "E178.left", {"start": v(69.45, -6) * mm, "end": v(69.45, -22.18) * mm});
            skLineSegment(sketch, "E178.right", {"start": v(135, -6) * mm, "end": v(135, -8.5) * mm});
            skLineSegment(sketch, "E179", {"start": v(66.79, -24.07) * mm, "end": v(66.85, -24.03) * mm});
            skLineSegment(sketch, "E180", {"start": v(92.19, -6) * mm, "end": v(129.84, -25.35) * mm});
            skLineSegment(sketch, "E181", {"start": v(129.84, -30.65) * mm, "end": v(92.19, -50) * mm});
            skLineSegment(sketch, "E182", {"start": v(92.19, -50) * mm, "end": v(72.46, -36.03) * mm});
            skArc(sketch, "E183", {"start": v(92.14, -21.44) * mm, "mid": v(89.19, -22.17) * mm, "end": v(86.88, -24.15) * mm});
            skFitSpline(sketch, "E184.trimOffspring", {"points": [v(92.19, -28) * mm, v(97.4, -24.03) * mm, v(87.93, -32.99) * mm, v(90.96, -27) * mm, v(92.19, -28) * mm]});
            skLineSegment(sketch, "E185.trimOffspring", {"start": v(96.44, -31.97) * mm, "end": v(101.02, -31.97) * mm});
            skLineSegment(sketch, "E186.trimOffspring", {"start": v(91.34, -30.5) * mm, "end": v(91.34, -30.5) * mm});
            skCircle(sketch, "E187", {"center": v(92.19, -28) * mm, "radius": 9.69 * mm});
            skArc(sketch, "E188.trimOffspring", {"start": v(86.45, -24.82) * mm, "mid": v(86.45, -24.82) * mm, "end": v(86.45, -24.82) * mm});
            skFitSpline(sketch, "E189.trimOffspring", {"points": [v(93.14, -21.51) * mm, v(92.19, -28) * mm, v(86.45, -24.82) * mm, v(95.97, -33.36) * mm, v(93.14, -21.51) * mm]});
            skArc(sketch, "E190.trimOffspring", {"start": v(86.1, -25.54) * mm, "mid": v(95, -33.92) * mm, "end": v(94.1, -21.73) * mm});
            skLineSegment(sketch, "E191.bottom", {"start": v(72.46, -24.03) * mm, "end": v(79.71, -24.03) * mm});
            skLineSegment(sketch, "E191.top", {"start": v(72.46, -31.97) * mm, "end": v(79.71, -31.97) * mm});
            skLineSegment(sketch, "E191.left", {"start": v(69.45, -24.03) * mm, "end": v(69.45, -31.97) * mm});
            skPoint(sketch, "E191.middle", {"position": v(91.73, -28) * mm});
            skPoint(sketch, "E191.middle.positionSnap0", {"position": v(69.45, -28) * mm});
            skPoint(sketch, "E191.cornerSnap0", {"position": v(69.45, -28) * mm});
            skPoint(sketch, "E191.centerSnap0", {"position": v(69.45, -28) * mm});
            skLineSegment(sketch, "E192", {"start": v(66.74, -25.88) * mm, "end": v(69.45, -23.95) * mm});
            skLineSegment(sketch, "E193", {"start": v(97.73, -8.85) * mm, "end": v(114.02, -24.03) * mm});
            skLineSegment(sketch, "E194", {"start": v(114.02, -31.97) * mm, "end": v(97.73, -47.15) * mm});
            skLineSegment(sketch, "E195", {"start": v(135, -31.97) * mm, "end": v(114.02, -42.75) * mm});
            skPoint(sketch, "E195.endSnap0", {"position": v(102.22, -50) * mm});
            skLineSegment(sketch, "E196", {"start": v(99.92, -50) * mm, "end": v(110.33, -44.65) * mm});
            skLineSegment(sketch, "E197", {"start": v(135, -24.03) * mm, "end": v(114.02, -13.25) * mm});
            skLineSegment(sketch, "E198.trimOffspring", {"start": v(69.45, -23.95) * mm, "end": v(69.45, -32.05) * mm, "construction": true});
            skLineSegment(sketch, "E199.trimOffspring", {"start": v(69.45, -33.9) * mm, "end": v(69.45, -53.04) * mm, "construction": true});
            skLineSegment(sketch, "E200.trimOffspring", {"start": v(69.45, -33.9) * mm, "end": v(69.45, -50) * mm});
            skLineSegment(sketch, "E201.trimOffspring", {"start": v(69.45, -32.05) * mm, "end": v(66.74, -30.12) * mm});
            skLineSegment(sketch, "E202.trimOffspring", {"start": v(69.45, -23.95) * mm, "end": v(69.45, -32.05) * mm});
            skLineSegment(sketch, "E203.trimOffspring", {"start": v(69.34, -24.03) * mm, "end": v(69.45, -24.03) * mm});
            skLineSegment(sketch, "E204.trimOffspring", {"start": v(72.46, -20.04) * mm, "end": v(92.19, -6) * mm});
            skLineSegment(sketch, "E205", {"start": v(129.84, -25.35) * mm, "end": v(114.02, -24.03) * mm});
            skLineSegment(sketch, "E206", {"start": v(114.02, -31.97) * mm, "end": v(129.84, -30.65) * mm});
            skLineSegment(sketch, "E207", {"start": v(117.46, -15.01) * mm, "end": v(126.23, -10.5) * mm});
            skLineSegment(sketch, "E208", {"start": v(117.46, -40.99) * mm, "end": v(126.23, -45.5) * mm});
            skLineSegment(sketch, "E209", {"start": v(126.23, -45.5) * mm, "end": v(114.02, -46.51) * mm});
            skLineSegment(sketch, "E210", {"start": v(114.02, -46.51) * mm, "end": v(114.02, -42.75) * mm});
            skLineSegment(sketch, "E211", {"start": v(114.02, -42.75) * mm, "end": v(114.02, -46.51) * mm});
            skLineSegment(sketch, "E212", {"start": v(114.02, -50) * mm, "end": v(114.02, -48.72) * mm});
            skLineSegment(sketch, "E213", {"start": v(110.33, -6) * mm, "end": v(110.33, -11.35) * mm});
            skLineSegment(sketch, "E214.trimOffspring", {"start": v(110.33, -44.65) * mm, "end": v(110.33, -50) * mm});
            skLineSegment(sketch, "E215.trimOffspring", {"start": v(114.02, -42.75) * mm, "end": v(135, -31.97) * mm});
            skLineSegment(sketch, "E216.trimOffspring", {"start": v(114.02, -50) * mm, "end": v(135, -50) * mm});
            skLineSegment(sketch, "E217.trimOffspring", {"start": v(114.02, -13.25) * mm, "end": v(114.02, -9.49) * mm});
            skLineSegment(sketch, "E218.trimOffspring", {"start": v(110.33, -11.35) * mm, "end": v(99.92, -6) * mm});
            skLineSegment(sketch, "E219", {"start": v(126.23, -10.5) * mm, "end": v(114.02, -9.49) * mm});
            skLineSegment(sketch, "E220.trimOffspring", {"start": v(99.92, -6) * mm, "end": v(110.33, -6) * mm});
            skPoint(sketch, "E221.orphan", {"position": v(94.67, -50) * mm});
            skLineSegment(sketch, "E222.trimOffspring", {"start": v(99.92, -50) * mm, "end": v(110.33, -50) * mm});
            skLineSegment(sketch, "E223.trimOffspring", {"start": v(110.33, -44.65) * mm, "end": v(99.92, -50) * mm});
            skLineSegment(sketch, "E224.trimOffspring", {"start": v(114.02, -6) * mm, "end": v(135, -6) * mm});
            skLineSegment(sketch, "E225", {"start": v(114.02, -7.28) * mm, "end": v(129.92, -8.6) * mm});
            skLineSegment(sketch, "E226", {"start": v(114.02, -48.72) * mm, "end": v(130.73, -47.33) * mm});
            skPoint(sketch, "E226.endSnap0", {"position": v(105.12, -47.33) * mm});
            skLineSegment(sketch, "E227.trimOffspring", {"start": v(129.92, -8.6) * mm, "end": v(135, -6) * mm});
            skLineSegment(sketch, "E228.trimOffspring", {"start": v(114.02, -7.28) * mm, "end": v(114.02, -6) * mm});
            skLineSegment(sketch, "E229.trimOffspring", {"start": v(129.92, -47.4) * mm, "end": v(135, -50) * mm});
            skLineSegment(sketch, "E230.trimOffspring", {"start": v(114.02, -48.72) * mm, "end": v(114.02, -50) * mm});
            skLineSegment(sketch, "E231", {"start": v(122.34, -15.01) * mm, "end": v(133.08, -9.5) * mm});
            skLineSegment(sketch, "E232", {"start": v(133.08, -9.5) * mm, "end": v(122.34, -15.01) * mm});
            skLineSegment(sketch, "E233", {"start": v(122.34, -15.01) * mm, "end": v(133.08, -20.54) * mm});
            skLineSegment(sketch, "E234", {"start": v(122.34, -40.99) * mm, "end": v(133.08, -35.46) * mm});
            skLineSegment(sketch, "E235", {"start": v(133.08, -35.46) * mm, "end": v(122.34, -40.99) * mm});
            skLineSegment(sketch, "E236", {"start": v(122.34, -40.99) * mm, "end": v(133.08, -46.5) * mm});
            skLineSegment(sketch, "E237.trimOffspring", {"start": v(129.02, -30.72) * mm, "end": v(128.67, -31.25) * mm});
            skLineSegment(sketch, "E238.trimOffspring", {"start": v(135, -47.5) * mm, "end": v(135, -50) * mm});
            skLineSegment(sketch, "E239.trimOffspring", {"start": v(135, -21.52) * mm, "end": v(135, -34.48) * mm});
            skLineSegment(sketch, "E240", {"start": v(133.08, -9.5) * mm, "end": v(133.08, -20.54) * mm});
            skLineSegment(sketch, "E241", {"start": v(133.08, -35.46) * mm, "end": v(133.08, -46.5) * mm});
            skPoint(sketch, "E242.orphan", {"position": v(94.67, -7.28) * mm});
            skPoint(sketch, "E243.trimOffspring.end.orphan", {"position": v(94.67, -48.72) * mm});
            skPoint(sketch, "E177.right.end.orphan", {"position": v(203.26, -24.03) * mm});
            skPoint(sketch, "E177.right.start.orphan", {"position": v(203.26, -31.97) * mm});
            skLineSegment(sketch, "E244.trimOffspring", {"start": v(97.39, -24.03) * mm, "end": v(97.4, -24.03) * mm});
            skCircle(sketch, "E245", {"center": v(92.19, -28) * mm, "radius": 6.55 * mm});
            skLineSegment(sketch, "E246", {"start": v(72.46, -6) * mm, "end": v(72.46, -20.04) * mm});
            skLineSegment(sketch, "E247", {"start": v(72.46, -24.03) * mm, "end": v(72.46, -31.97) * mm});
            skLineSegment(sketch, "E248", {"start": v(79.71, -24.03) * mm, "end": v(79.71, -31.97) * mm});
            skLineSegment(sketch, "E249", {"start": v(79.71, -31.97) * mm, "end": v(72.46, -31.97) * mm});
            skPoint(sketch, "E250.startSnap0", {"position": v(79.71, -28) * mm});
            skLineSegment(sketch, "E251", {"start": v(107.47, -28) * mm, "end": v(102.32, -37.58) * mm});
            skLineSegment(sketch, "E252", {"start": v(102.32, -37.58) * mm, "end": v(115.04, -28) * mm});
            skLineSegment(sketch, "E253", {"start": v(115.04, -28) * mm, "end": v(102.32, -21.15) * mm});
            skLineSegment(sketch, "E254", {"start": v(107.47, -28) * mm, "end": v(102.32, -21.15) * mm});
            skPoint(sketch, "E255.orphan", {"position": v(119.48, -28) * mm});
            skLineSegment(sketch, "E256.trimOffspring", {"start": v(72.46, -36.03) * mm, "end": v(72.46, -50) * mm});
            skLineSegment(sketch, "E257.trimOffspring", {"start": v(69.45, -33.9) * mm, "end": v(66.74, -31.97) * mm});
            skLineSegment(sketch, "E258.trimOffspring", {"start": v(83.35, -31.97) * mm, "end": v(86.97, -31.97) * mm});
            skLineSegment(sketch, "E259.trimOffspring", {"start": v(83.35, -24.03) * mm, "end": v(86.97, -24.03) * mm});
            skLineSegment(sketch, "E260.trimOffspring", {"start": v(83.35, -31.97) * mm, "end": v(97.4, -31.97) * mm});
            skLineSegment(sketch, "E261", {"start": v(83.35, -24.03) * mm, "end": v(101.02, -24.03) * mm});
            skSolve(sketch);
        }
        {
            var Q0;
            {var subQ2=sQuery(id+"F11.wireOp",EDGE,"E193");Q0=makeQuery(id+"F11.imprint","IMPRINT",FACE,{"disambiguationData":[TD([[makeQuery(id+"F11.imprint","IMPRINT",EDGE,{"derivedFrom":subQ2}),1.0]])]});}
            var Q1;
            {var subQ0=sQuery(id+"F11.wireOp",EDGE,"E194");Q1=makeQuery(id+"F11.imprint","IMPRINT",FACE,{"disambiguationData":[TD([[makeQuery(id+"F11.imprint","IMPRINT",EDGE,{"derivedFrom":subQ0}),1.0]])]});}
            var Q2;
            Q2=makeQuery(id+"F11.imprint","IMPRINT",FACE,{"disambiguationData":[TD([[makeQuery(id+"F11.imprint","IMPRINT",EDGE,{"derivedFrom":sQuery(id+"F11.wireOp",EDGE,"E235")}),1.0]])]});
            var Q3;
            Q3=makeQuery(id+"F11.imprint","IMPRINT",FACE,{"disambiguationData":[TD([[makeQuery(id+"F11.imprint","IMPRINT",EDGE,{"derivedFrom":sQuery(id+"F11.wireOp",EDGE,"E232")}),1.0]])]});
            var Q4;
            Q4=makeQuery(id+"F11.imprint","IMPRINT",FACE,{"disambiguationData":[TD([[makeQuery(id+"F11.imprint","IMPRINT",EDGE,{"derivedFrom":sQuery(id+"F11.wireOp",EDGE,"E224.trimOffspring")}),-1.0]])]});
            var Q5;
            {var subQ2=sQuery(id+"F11.wireOp",EDGE,"E207");Q5=makeQuery(id+"F11.imprint","IMPRINT",FACE,{"disambiguationData":[TD([[makeQuery(id+"F11.imprint","IMPRINT",EDGE,{"derivedFrom":subQ2}),1.0]])]});}
            var Q6;
            {var subQ0=sQuery(id+"F11.wireOp",EDGE,"E208");Q6=makeQuery(id+"F11.imprint","IMPRINT",FACE,{"disambiguationData":[TD([[makeQuery(id+"F11.imprint","IMPRINT",EDGE,{"derivedFrom":subQ0}),-1.0]])]});}
            var Q7;
            Q7=makeQuery(id+"F11.imprint","IMPRINT",FACE,{"disambiguationData":[TD([[makeQuery(id+"F11.imprint","IMPRINT",EDGE,{"derivedFrom":sQuery(id+"F11.wireOp",EDGE,"E216.trimOffspring")}),1.0]])]});
            var Q8;
            Q8=makeQuery(id+"F11.imprint","IMPRINT",FACE,{"disambiguationData":[TD([[makeQuery(id+"F11.imprint","IMPRINT",EDGE,{"derivedFrom":sQuery(id+"F11.wireOp",EDGE,"E214.trimOffspring")}),-1.0]])]});
            var Q9;
            Q9=makeQuery(id+"F11.imprint","IMPRINT",FACE,{"disambiguationData":[TD([[makeQuery(id+"F11.imprint","IMPRINT",EDGE,{"derivedFrom":sQuery(id+"F11.wireOp",EDGE,"E213")}),-1.0]])]});
            var Q10;
            {var subQ1=sQuery(id+"F11.wireOp",EDGE,"E184.trimOffspring");Q10=makeQuery(id+"F11.imprint","IMPRINT",FACE,{"disambiguationData":[TD([[makeQuery(id+"F11.imprint","IMPRINT",EDGE,{"derivedFrom":subQ1}),1.0]])]});}
            var Q11;
            {var subQ3=sQuery(id+"F11.wireOp",EDGE,"E203.trimOffspring");var subQ5=makeQuery(id+"F11.imprint","IMPRINT",VERTEX,{"derivedFrom":subQ3});Q11=makeQuery(id+"F11.imprint","IMPRINT",FACE,{"disambiguationData":[TD([[makeQuery(id+"F11.imprint","IMPRINT",EDGE,{"disambiguationData":[TD([[subQ5,1.0]])],"derivedFrom":subQ3}),1.0]])]});}
            var Q12;
            {var subQ3=sQuery(id+"F11.wireOp",EDGE,"E261");var subQ11=makeQuery(id+"F11.imprint","IMPRINT",VERTEX,{"derivedFrom":subQ3});Q12=makeQuery(id+"F11.imprint","IMPRINT",FACE,{"disambiguationData":[TD([[makeQuery(id+"F11.imprint","IMPRINT",EDGE,{"disambiguationData":[TD([[subQ11,1.0]])],"derivedFrom":subQ3}),1.0]])]});}
            var Q13;
            Q13=makeQuery(id+"F11.imprint","IMPRINT",FACE,{"disambiguationData":[TD([[makeQuery(id+"F11.imprint","IMPRINT",EDGE,{"derivedFrom":sQuery(id+"F11.wireOp",EDGE,"E247")}),1.0]])]});
            var Q14;
            Q14=makeQuery(id+"F11.imprint","IMPRINT",FACE,{"disambiguationData":[TD([[makeQuery(id+"F11.imprint","IMPRINT",EDGE,{"derivedFrom":sQuery(id+"F11.wireOp",EDGE,"E178.top")}),1.0]])]});
            var Q15;
            Q15=makeQuery(id+"F11.imprint","IMPRINT",FACE,{"disambiguationData":[TD([[makeQuery(id+"F11.imprint","IMPRINT",EDGE,{"derivedFrom":sQuery(id+"F11.wireOp",EDGE,"E178.bottom")}),-1.0]])]});
            var Q16;
            {var subQ4=sQuery(id+"F11.wireOp",EDGE,"E177.bottom");Q16=makeQuery(id+"F11.imprint","IMPRINT",FACE,{"disambiguationData":[TD([[makeQuery(id+"F11.imprint","IMPRINT",EDGE,{"derivedFrom":subQ4}),1.0]])]});}
            var Q17;
            {var subQ0=sQuery(id+"F11.wireOp",EDGE,"E261");var subQ1=sQuery(id+"F11.wireOp",EDGE,"E184.trimOffspring");var subQ2=makeQuery(id+"F11.imprint","INTERSECT",VERTEX,{"derivedFrom":[subQ1,subQ0]});Q17=makeQuery(id+"F11.imprint","IMPRINT",FACE,{"disambiguationData":[TD([[makeQuery(id+"F11.imprint","IMPRINT",EDGE,{"disambiguationData":[TD([[subQ2,-1.0]])],"derivedFrom":subQ1}),1.0]])]});}
            var Q18;
            {var subQ0=sQuery(id+"F11.wireOp",EDGE,"E260.trimOffspring");var subQ4=makeQuery(id+"F11.imprint","IMPRINT",VERTEX,{"derivedFrom":subQ0});Q18=makeQuery(id+"F11.imprint","IMPRINT",FACE,{"disambiguationData":[TD([[makeQuery(id+"F11.imprint","IMPRINT",EDGE,{"disambiguationData":[TD([[subQ4,1.0]])],"derivedFrom":subQ0}),-1.0]])]});}
            extrude(context, id + "F12", {"entities" : qUnion([Q0, Q1, Q2, Q3, Q4, Q5, Q6, Q7, Q8, Q9, Q10, Q11, Q12, Q13, Q14, Q15, Q16, Q17, Q18]), "operationType" : NewBodyOperationType.REMOVE, "endBound" : BoundingType.THROUGH_ALL, "oppositeDirection" : true, "depth" : 25 * mm});
        }
        {
            var Q0;
            {var subQ0=sQuery(id+"F0.wireOp",EDGE,"E12.bottom");Q0=makeQuery(id+"F8.boolean.opBoolean","INTERSECT",EDGE,{"derivedFrom":[makeQuery(id+"F6.boolean.opBoolean","MERGE",FACE,{"derivedFrom":[makeQuery(id+"F1.opExtrude","SWEPT_FACE",FACE,{"disambiguationData":[OSD([subQ0])]}),makeQuery(id+"F6.opExtrude","SWEPT_FACE",FACE,{"disambiguationData":[OSD([subQ0])]})]}),makeQuery(id+"F8.opExtrude","SWEPT_FACE",FACE,{"disambiguationData":[OSD([sQuery(id+"F7.wireOp",EDGE,"E88.top")])]})]});}
            var Q1;
            Q1=makeQuery(id+"F6.opExtrude","CAP_EDGE",EDGE,{"disambiguationData":[OSD([sQuery(id+"F0.wireOp",EDGE,"E12.bottom")])],"isStart":false});
            var Q2;
            Q2=makeQuery(id+"F6.opExtrude","CAP_EDGE",EDGE,{"disambiguationData":[OSD([sQuery(id+"F0.wireOp",EDGE,"E81.trimOffspring")])],"isStart":false});
            var Q3;
            Q3=makeQuery(id+"F6.opExtrude","CAP_EDGE",EDGE,{"disambiguationData":[OSD([sQuery(id+"F0.wireOp",EDGE,"E34.bottom"),sQuery(id+"F0.wireOp",EDGE,"E78")])],"isStart":false});
            var Q4;
            {var subQ0=sQuery(id+"F0.wireOp",EDGE,"E78");var subQ1=sQuery(id+"F0.wireOp",EDGE,"E34.bottom");Q4=makeQuery(id+"F8.boolean.opBoolean","INTERSECT",EDGE,{"derivedFrom":[makeQuery(id+"F6.boolean.opBoolean","MERGE",FACE,{"derivedFrom":[makeQuery(id+"F1.opExtrude","SWEPT_FACE",FACE,{"disambiguationData":[OSD([subQ1,subQ0])]}),makeQuery(id+"F6.opExtrude","SWEPT_FACE",FACE,{"disambiguationData":[OSD([subQ1,subQ0])]})]}),makeQuery(id+"F8.opExtrude","SWEPT_FACE",FACE,{"disambiguationData":[OSD([sQuery(id+"F7.wireOp",EDGE,"E88.top")])]})]});}
            var Q5;
            {var subQ0=sQuery(id+"F0.wireOp",EDGE,"E78");var subQ1=sQuery(id+"F0.wireOp",EDGE,"E34.bottom");Q5=makeQuery(id+"F8.boolean.opBoolean","INTERSECT",EDGE,{"derivedFrom":[makeQuery(id+"F6.boolean.opBoolean","MERGE",FACE,{"derivedFrom":[makeQuery(id+"F1.opExtrude","SWEPT_FACE",FACE,{"disambiguationData":[OSD([subQ1,subQ0])]}),makeQuery(id+"F6.opExtrude","SWEPT_FACE",FACE,{"disambiguationData":[OSD([subQ1,subQ0])]})]}),makeQuery(id+"F8.opExtrude","SWEPT_FACE",FACE,{"disambiguationData":[OSD([sQuery(id+"F7.wireOp",EDGE,"E91.bottom")])]})]});}
            var Q6;
            {var subQ0=sQuery(id+"F0.wireOp",EDGE,"E78");var subQ1=sQuery(id+"F0.wireOp",EDGE,"E34.bottom");Q6=makeQuery(id+"F8.boolean.opBoolean","INTERSECT",EDGE,{"derivedFrom":[makeQuery(id+"F6.boolean.opBoolean","MERGE",FACE,{"derivedFrom":[makeQuery(id+"F1.opExtrude","SWEPT_FACE",FACE,{"disambiguationData":[OSD([subQ1,subQ0])]}),makeQuery(id+"F6.opExtrude","SWEPT_FACE",FACE,{"disambiguationData":[OSD([subQ1,subQ0])]})]}),makeQuery(id+"F8.opExtrude","SWEPT_FACE",FACE,{"disambiguationData":[OSD([sQuery(id+"F7.wireOp",EDGE,"E91.top")])]})]});}
            var Q7;
            {var subQ0=sQuery(id+"F0.wireOp",EDGE,"E81.trimOffspring");Q7=makeQuery(id+"F8.boolean.opBoolean","INTERSECT",EDGE,{"derivedFrom":[makeQuery(id+"F6.boolean.opBoolean","MERGE",FACE,{"derivedFrom":[makeQuery(id+"F1.opExtrude","SWEPT_FACE",FACE,{"disambiguationData":[OSD([subQ0])]}),makeQuery(id+"F6.opExtrude","SWEPT_FACE",FACE,{"disambiguationData":[OSD([subQ0])]})]}),makeQuery(id+"F8.opExtrude","SWEPT_FACE",FACE,{"disambiguationData":[OSD([sQuery(id+"F7.wireOp",EDGE,"E91.top")])]})]});}
            var Q8;
            {var subQ0=sQuery(id+"F0.wireOp",EDGE,"E81.trimOffspring");Q8=makeQuery(id+"F8.boolean.opBoolean","INTERSECT",EDGE,{"derivedFrom":[makeQuery(id+"F6.boolean.opBoolean","MERGE",FACE,{"derivedFrom":[makeQuery(id+"F1.opExtrude","SWEPT_FACE",FACE,{"disambiguationData":[OSD([subQ0])]}),makeQuery(id+"F6.opExtrude","SWEPT_FACE",FACE,{"disambiguationData":[OSD([subQ0])]})]}),makeQuery(id+"F8.opExtrude","SWEPT_FACE",FACE,{"disambiguationData":[OSD([sQuery(id+"F7.wireOp",EDGE,"E91.bottom")])]})]});}
            var Q9;
            {var subQ0=sQuery(id+"F0.wireOp",EDGE,"E81.trimOffspring");Q9=makeQuery(id+"F8.boolean.opBoolean","INTERSECT",EDGE,{"derivedFrom":[makeQuery(id+"F6.boolean.opBoolean","MERGE",FACE,{"derivedFrom":[makeQuery(id+"F1.opExtrude","SWEPT_FACE",FACE,{"disambiguationData":[OSD([subQ0])]}),makeQuery(id+"F6.opExtrude","SWEPT_FACE",FACE,{"disambiguationData":[OSD([subQ0])]})]}),makeQuery(id+"F8.opExtrude","SWEPT_FACE",FACE,{"disambiguationData":[OSD([sQuery(id+"F7.wireOp",EDGE,"E88.top")])]})]});}
            var Q10;
            {var subQ0=sQuery(id+"F0.wireOp",EDGE,"E78");var subQ1=sQuery(id+"F0.wireOp",EDGE,"E34.bottom");Q10=makeQuery(id+"F8.boolean.opBoolean","INTERSECT",EDGE,{"derivedFrom":[makeQuery(id+"F6.boolean.opBoolean","MERGE",FACE,{"derivedFrom":[makeQuery(id+"F1.opExtrude","SWEPT_FACE",FACE,{"disambiguationData":[OSD([subQ1,subQ0])]}),makeQuery(id+"F6.opExtrude","SWEPT_FACE",FACE,{"disambiguationData":[OSD([subQ1,subQ0])]})]}),makeQuery(id+"F8.opExtrude","SWEPT_FACE",FACE,{"disambiguationData":[OSD([sQuery(id+"F7.wireOp",EDGE,"E89.top")])]})]});}
            var Q11;
            Q11=makeQuery(id+"F1.opExtrude","CAP_EDGE",EDGE,{"disambiguationData":[OSD([sQuery(id+"F0.wireOp",EDGE,"E34.bottom"),sQuery(id+"F0.wireOp",EDGE,"E78")])],"isStart":true});
            var Q12;
            Q12=makeQuery(id+"F1.opExtrude","CAP_EDGE",EDGE,{"disambiguationData":[OSD([sQuery(id+"F0.wireOp",EDGE,"E81.trimOffspring")])],"isStart":true});
            var Q13;
            {var subQ0=sQuery(id+"F0.wireOp",EDGE,"E81.trimOffspring");Q13=makeQuery(id+"F8.boolean.opBoolean","INTERSECT",EDGE,{"derivedFrom":[makeQuery(id+"F6.boolean.opBoolean","MERGE",FACE,{"derivedFrom":[makeQuery(id+"F1.opExtrude","SWEPT_FACE",FACE,{"disambiguationData":[OSD([subQ0])]}),makeQuery(id+"F6.opExtrude","SWEPT_FACE",FACE,{"disambiguationData":[OSD([subQ0])]})]}),makeQuery(id+"F8.opExtrude","SWEPT_FACE",FACE,{"disambiguationData":[OSD([sQuery(id+"F7.wireOp",EDGE,"E89.top")])]})]});}
            var Q14;
            {var subQ0=sQuery(id+"F0.wireOp",EDGE,"E12.bottom");Q14=makeQuery(id+"F8.boolean.opBoolean","INTERSECT",EDGE,{"derivedFrom":[makeQuery(id+"F6.boolean.opBoolean","MERGE",FACE,{"derivedFrom":[makeQuery(id+"F1.opExtrude","SWEPT_FACE",FACE,{"disambiguationData":[OSD([subQ0])]}),makeQuery(id+"F6.opExtrude","SWEPT_FACE",FACE,{"disambiguationData":[OSD([subQ0])]})]}),makeQuery(id+"F8.opExtrude","SWEPT_FACE",FACE,{"disambiguationData":[OSD([sQuery(id+"F7.wireOp",EDGE,"E89.top")])]})]});}
            var Q15;
            Q15=makeQuery(id+"F6.opExtrude","CAP_EDGE",EDGE,{"disambiguationData":[OSD([sQuery(id+"F0.wireOp",EDGE,"E12.bottom")])],"isStart":true});
            var Q16;
            {var subQ0=sQuery(id+"F0.wireOp",EDGE,"E12.bottom");Q16=makeQuery(id+"F8.boolean.opBoolean","INTERSECT",EDGE,{"derivedFrom":[makeQuery(id+"F6.boolean.opBoolean","MERGE",FACE,{"derivedFrom":[makeQuery(id+"F1.opExtrude","SWEPT_FACE",FACE,{"disambiguationData":[OSD([subQ0])]}),makeQuery(id+"F6.opExtrude","SWEPT_FACE",FACE,{"disambiguationData":[OSD([subQ0])]})]}),makeQuery(id+"F8.opExtrude","SWEPT_FACE",FACE,{"disambiguationData":[OSD([sQuery(id+"F7.wireOp",EDGE,"E91.top")])]})]});}
            var Q17;
            {var subQ0=sQuery(id+"F0.wireOp",EDGE,"E12.bottom");Q17=makeQuery(id+"F8.boolean.opBoolean","INTERSECT",EDGE,{"derivedFrom":[makeQuery(id+"F6.boolean.opBoolean","MERGE",FACE,{"derivedFrom":[makeQuery(id+"F1.opExtrude","SWEPT_FACE",FACE,{"disambiguationData":[OSD([subQ0])]}),makeQuery(id+"F6.opExtrude","SWEPT_FACE",FACE,{"disambiguationData":[OSD([subQ0])]})]}),makeQuery(id+"F8.opExtrude","SWEPT_FACE",FACE,{"disambiguationData":[OSD([sQuery(id+"F7.wireOp",EDGE,"E91.bottom")])]})]});}
            var Q18;
            {var subQ0=sQuery(id+"F0.wireOp",EDGE,"E14");Q18=makeQuery(id+"F8.boolean.opBoolean","INTERSECT",EDGE,{"derivedFrom":[makeQuery(id+"F6.boolean.opBoolean","MERGE",FACE,{"derivedFrom":[makeQuery(id+"F1.opExtrude","SWEPT_FACE",FACE,{"disambiguationData":[OSD([subQ0])]}),makeQuery(id+"F6.opExtrude","SWEPT_FACE",FACE,{"disambiguationData":[OSD([subQ0])]})]}),makeQuery(id+"F8.opExtrude","SWEPT_FACE",FACE,{"disambiguationData":[OSD([sQuery(id+"F7.wireOp",EDGE,"E91.bottom")])]})]});}
            var Q19;
            {var subQ0=sQuery(id+"F0.wireOp",EDGE,"E14");Q19=makeQuery(id+"F8.boolean.opBoolean","INTERSECT",EDGE,{"derivedFrom":[makeQuery(id+"F6.boolean.opBoolean","MERGE",FACE,{"derivedFrom":[makeQuery(id+"F1.opExtrude","SWEPT_FACE",FACE,{"disambiguationData":[OSD([subQ0])]}),makeQuery(id+"F6.opExtrude","SWEPT_FACE",FACE,{"disambiguationData":[OSD([subQ0])]})]}),makeQuery(id+"F8.opExtrude","SWEPT_FACE",FACE,{"disambiguationData":[OSD([sQuery(id+"F7.wireOp",EDGE,"E91.top")])]})]});}
            var Q20;
            {var subQ0=sQuery(id+"F0.wireOp",EDGE,"E14");Q20=makeQuery(id+"F8.boolean.opBoolean","INTERSECT",EDGE,{"derivedFrom":[makeQuery(id+"F6.boolean.opBoolean","MERGE",FACE,{"derivedFrom":[makeQuery(id+"F1.opExtrude","SWEPT_FACE",FACE,{"disambiguationData":[OSD([subQ0])]}),makeQuery(id+"F6.opExtrude","SWEPT_FACE",FACE,{"disambiguationData":[OSD([subQ0])]})]}),makeQuery(id+"F8.opExtrude","SWEPT_FACE",FACE,{"disambiguationData":[OSD([sQuery(id+"F7.wireOp",EDGE,"E88.top")])]})]});}
            var Q21;
            Q21=makeQuery(id+"F6.opExtrude","CAP_EDGE",EDGE,{"disambiguationData":[OSD([sQuery(id+"F0.wireOp",EDGE,"E14")])],"isStart":false});
            var Q22;
            {var subQ0=sQuery(id+"F0.wireOp",EDGE,"E14");Q22=makeQuery(id+"F8.boolean.opBoolean","INTERSECT",EDGE,{"derivedFrom":[makeQuery(id+"F6.boolean.opBoolean","MERGE",FACE,{"derivedFrom":[makeQuery(id+"F1.opExtrude","SWEPT_FACE",FACE,{"disambiguationData":[OSD([subQ0])]}),makeQuery(id+"F6.opExtrude","SWEPT_FACE",FACE,{"disambiguationData":[OSD([subQ0])]})]}),makeQuery(id+"F8.opExtrude","SWEPT_FACE",FACE,{"disambiguationData":[OSD([sQuery(id+"F7.wireOp",EDGE,"E89.top")])]})]});}
            var Q23;
            Q23=makeQuery(id+"F6.opExtrude","CAP_EDGE",EDGE,{"disambiguationData":[OSD([sQuery(id+"F0.wireOp",EDGE,"E14")])],"isStart":true});
            var Q24;
            Q24=makeQuery(id+"F1.opExtrude","CAP_EDGE",EDGE,{"disambiguationData":[OSD([sQuery(id+"F0.wireOp",EDGE,"E19.top")])],"isStart":true});
            var Q25;
            {var subQ0=sQuery(id+"F0.wireOp",EDGE,"E19.top");Q25=makeQuery(id+"F8.boolean.opBoolean","INTERSECT",EDGE,{"derivedFrom":[makeQuery(id+"F6.boolean.opBoolean","MERGE",FACE,{"derivedFrom":[makeQuery(id+"F1.opExtrude","SWEPT_FACE",FACE,{"disambiguationData":[OSD([subQ0])]}),makeQuery(id+"F6.opExtrude","SWEPT_FACE",FACE,{"disambiguationData":[OSD([subQ0])]})]}),makeQuery(id+"F8.opExtrude","SWEPT_FACE",FACE,{"disambiguationData":[OSD([sQuery(id+"F7.wireOp",EDGE,"E89.top")])]})]});}
            var Q26;
            {var subQ0=sQuery(id+"F0.wireOp",EDGE,"E19.top");Q26=makeQuery(id+"F8.boolean.opBoolean","INTERSECT",EDGE,{"derivedFrom":[makeQuery(id+"F6.boolean.opBoolean","MERGE",FACE,{"derivedFrom":[makeQuery(id+"F1.opExtrude","SWEPT_FACE",FACE,{"disambiguationData":[OSD([subQ0])]}),makeQuery(id+"F6.opExtrude","SWEPT_FACE",FACE,{"disambiguationData":[OSD([subQ0])]})]}),makeQuery(id+"F8.opExtrude","SWEPT_FACE",FACE,{"disambiguationData":[OSD([sQuery(id+"F7.wireOp",EDGE,"E91.top")])]})]});}
            var Q27;
            {var subQ0=sQuery(id+"F0.wireOp",EDGE,"E19.top");Q27=makeQuery(id+"F8.boolean.opBoolean","INTERSECT",EDGE,{"derivedFrom":[makeQuery(id+"F6.boolean.opBoolean","MERGE",FACE,{"derivedFrom":[makeQuery(id+"F1.opExtrude","SWEPT_FACE",FACE,{"disambiguationData":[OSD([subQ0])]}),makeQuery(id+"F6.opExtrude","SWEPT_FACE",FACE,{"disambiguationData":[OSD([subQ0])]})]}),makeQuery(id+"F8.opExtrude","SWEPT_FACE",FACE,{"disambiguationData":[OSD([sQuery(id+"F7.wireOp",EDGE,"E91.bottom")])]})]});}
            var Q28;
            {var subQ0=sQuery(id+"F0.wireOp",EDGE,"E19.top");Q28=makeQuery(id+"F8.boolean.opBoolean","INTERSECT",EDGE,{"derivedFrom":[makeQuery(id+"F6.boolean.opBoolean","MERGE",FACE,{"derivedFrom":[makeQuery(id+"F1.opExtrude","SWEPT_FACE",FACE,{"disambiguationData":[OSD([subQ0])]}),makeQuery(id+"F6.opExtrude","SWEPT_FACE",FACE,{"disambiguationData":[OSD([subQ0])]})]}),makeQuery(id+"F8.opExtrude","SWEPT_FACE",FACE,{"disambiguationData":[OSD([sQuery(id+"F7.wireOp",EDGE,"E88.top")])]})]});}
            var Q29;
            Q29=makeQuery(id+"F6.opExtrude","CAP_EDGE",EDGE,{"disambiguationData":[OSD([sQuery(id+"F0.wireOp",EDGE,"E19.top")])],"isStart":false});
            var Q30;
            Q30=makeQuery(id+"F6.opExtrude","CAP_EDGE",EDGE,{"disambiguationData":[OSD([sQuery(id+"F0.wireOp",EDGE,"E76")])],"isStart":false});
            var Q31;
            Q31=makeQuery(id+"F8.boolean.opBoolean","COPY",EDGE,{"derivedFrom":makeQuery(id+"F8.opExtrude","CAP_EDGE",EDGE,{"disambiguationData":[OSD([sQuery(id+"F7.wireOp",EDGE,"E88.top")])],"isStart":true})});
            var Q32;
            Q32=makeQuery(id+"F8.boolean.opBoolean","COPY",EDGE,{"derivedFrom":makeQuery(id+"F8.opExtrude","CAP_EDGE",EDGE,{"disambiguationData":[OSD([sQuery(id+"F7.wireOp",EDGE,"E91.bottom")])],"isStart":true})});
            var Q33;
            Q33=makeQuery(id+"F8.boolean.opBoolean","COPY",EDGE,{"derivedFrom":makeQuery(id+"F8.opExtrude","CAP_EDGE",EDGE,{"disambiguationData":[OSD([sQuery(id+"F7.wireOp",EDGE,"E91.top")])],"isStart":true})});
            var Q34;
            Q34=makeQuery(id+"F8.boolean.opBoolean","COPY",EDGE,{"derivedFrom":makeQuery(id+"F8.opExtrude","CAP_EDGE",EDGE,{"disambiguationData":[OSD([sQuery(id+"F7.wireOp",EDGE,"E89.top")])],"isStart":true})});
            var Q35;
            Q35=makeQuery(id+"F1.opExtrude","CAP_EDGE",EDGE,{"disambiguationData":[OSD([sQuery(id+"F0.wireOp",EDGE,"E76")])],"isStart":true});
            var Q36;
            {var subQ0=sQuery(id+"F0.wireOp",EDGE,"E5");Q36=makeQuery(id+"F8.boolean.opBoolean","INTERSECT",EDGE,{"derivedFrom":[makeQuery(id+"F6.boolean.opBoolean","MERGE",FACE,{"derivedFrom":[makeQuery(id+"F1.opExtrude","SWEPT_FACE",FACE,{"disambiguationData":[OSD([subQ0])]}),makeQuery(id+"F6.opExtrude","SWEPT_FACE",FACE,{"disambiguationData":[OSD([subQ0])]})]}),makeQuery(id+"F8.opExtrude","SWEPT_FACE",FACE,{"disambiguationData":[OSD([sQuery(id+"F7.wireOp",EDGE,"E91.top")])]})]});}
            var Q37;
            {var subQ0=sQuery(id+"F0.wireOp",EDGE,"E5");Q37=makeQuery(id+"F8.boolean.opBoolean","INTERSECT",EDGE,{"derivedFrom":[makeQuery(id+"F6.boolean.opBoolean","MERGE",FACE,{"derivedFrom":[makeQuery(id+"F1.opExtrude","SWEPT_FACE",FACE,{"disambiguationData":[OSD([subQ0])]}),makeQuery(id+"F6.opExtrude","SWEPT_FACE",FACE,{"disambiguationData":[OSD([subQ0])]})]}),makeQuery(id+"F8.opExtrude","SWEPT_FACE",FACE,{"disambiguationData":[OSD([sQuery(id+"F7.wireOp",EDGE,"E91.bottom")])]})]});}
            var Q38;
            {var subQ0=sQuery(id+"F0.wireOp",EDGE,"E5");Q38=makeQuery(id+"F8.boolean.opBoolean","INTERSECT",EDGE,{"derivedFrom":[makeQuery(id+"F6.boolean.opBoolean","MERGE",FACE,{"derivedFrom":[makeQuery(id+"F1.opExtrude","SWEPT_FACE",FACE,{"disambiguationData":[OSD([subQ0])]}),makeQuery(id+"F6.opExtrude","SWEPT_FACE",FACE,{"disambiguationData":[OSD([subQ0])]})]}),makeQuery(id+"F8.opExtrude","SWEPT_FACE",FACE,{"disambiguationData":[OSD([sQuery(id+"F7.wireOp",EDGE,"E89.top")])]})]});}
            var Q39;
            Q39=makeQuery(id+"F6.opExtrude","CAP_EDGE",EDGE,{"disambiguationData":[OSD([sQuery(id+"F0.wireOp",EDGE,"E5")])],"isStart":true});
            var Q40;
            {var subQ0=sQuery(id+"F0.wireOp",EDGE,"E5");Q40=makeQuery(id+"F8.boolean.opBoolean","INTERSECT",EDGE,{"derivedFrom":[makeQuery(id+"F6.boolean.opBoolean","MERGE",FACE,{"derivedFrom":[makeQuery(id+"F1.opExtrude","SWEPT_FACE",FACE,{"disambiguationData":[OSD([subQ0])]}),makeQuery(id+"F6.opExtrude","SWEPT_FACE",FACE,{"disambiguationData":[OSD([subQ0])]})]}),makeQuery(id+"F8.opExtrude","SWEPT_FACE",FACE,{"disambiguationData":[OSD([sQuery(id+"F7.wireOp",EDGE,"E88.top")])]})]});}
            var Q41;
            Q41=makeQuery(id+"F6.opExtrude","CAP_EDGE",EDGE,{"disambiguationData":[OSD([sQuery(id+"F0.wireOp",EDGE,"E5")])],"isStart":false});
            fillet(context, id + "F13", {"entities" : qUnion([Q0, Q1, Q2, Q3, Q4, Q5, Q6, Q7, Q8, Q9, Q10, Q11, Q12, Q13, Q14, Q15, Q16, Q17, Q18, Q19, Q20, Q21, Q22, Q23, Q24, Q25, Q26, Q27, Q28, Q29, Q30, Q31, Q32, Q33, Q34, Q35, Q36, Q37, Q38, Q39, Q40, Q41]), "radius" : 2 * mm, "tangentPropagation" : true, "allowEdgeOverflow" : false});
        }
        {
            var Q0;
            {var subQ0=sQuery(id+"F0.wireOp",EDGE,"E3");Q0=makeQuery(id+"F8.boolean.opBoolean","INTERSECT",EDGE,{"derivedFrom":[makeQuery(id+"F6.boolean.opBoolean","MERGE",FACE,{"derivedFrom":[makeQuery(id+"F1.opExtrude","SWEPT_FACE",FACE,{"disambiguationData":[OSD([subQ0])]}),makeQuery(id+"F6.opExtrude","SWEPT_FACE",FACE,{"disambiguationData":[OSD([subQ0])]})]}),makeQuery(id+"F8.opExtrude","SWEPT_FACE",FACE,{"disambiguationData":[OSD([sQuery(id+"F7.wireOp",EDGE,"E91.bottom")])]})]});}
            var Q1;
            {var subQ0=sQuery(id+"F0.wireOp",EDGE,"E3");Q1=makeQuery(id+"F8.boolean.opBoolean","INTERSECT",EDGE,{"derivedFrom":[makeQuery(id+"F6.boolean.opBoolean","MERGE",FACE,{"derivedFrom":[makeQuery(id+"F1.opExtrude","SWEPT_FACE",FACE,{"disambiguationData":[OSD([subQ0])]}),makeQuery(id+"F6.opExtrude","SWEPT_FACE",FACE,{"disambiguationData":[OSD([subQ0])]})]}),makeQuery(id+"F8.opExtrude","SWEPT_FACE",FACE,{"disambiguationData":[OSD([sQuery(id+"F7.wireOp",EDGE,"E89.top")])]})]});}
            var Q2;
            Q2=makeQuery(id+"F6.opExtrude","CAP_EDGE",EDGE,{"disambiguationData":[OSD([sQuery(id+"F0.wireOp",EDGE,"E3")])],"isStart":true});
            var Q3;
            {var subQ0=sQuery(id+"F0.wireOp",EDGE,"E3");Q3=makeQuery(id+"F8.boolean.opBoolean","INTERSECT",EDGE,{"derivedFrom":[makeQuery(id+"F6.boolean.opBoolean","MERGE",FACE,{"derivedFrom":[makeQuery(id+"F1.opExtrude","SWEPT_FACE",FACE,{"disambiguationData":[OSD([subQ0])]}),makeQuery(id+"F6.opExtrude","SWEPT_FACE",FACE,{"disambiguationData":[OSD([subQ0])]})]}),makeQuery(id+"F8.opExtrude","SWEPT_FACE",FACE,{"disambiguationData":[OSD([sQuery(id+"F7.wireOp",EDGE,"E91.top")])]})]});}
            var Q4;
            {var subQ0=sQuery(id+"F0.wireOp",EDGE,"E3");Q4=makeQuery(id+"F8.boolean.opBoolean","INTERSECT",EDGE,{"derivedFrom":[makeQuery(id+"F6.boolean.opBoolean","MERGE",FACE,{"derivedFrom":[makeQuery(id+"F1.opExtrude","SWEPT_FACE",FACE,{"disambiguationData":[OSD([subQ0])]}),makeQuery(id+"F6.opExtrude","SWEPT_FACE",FACE,{"disambiguationData":[OSD([subQ0])]})]}),makeQuery(id+"F8.opExtrude","SWEPT_FACE",FACE,{"disambiguationData":[OSD([sQuery(id+"F7.wireOp",EDGE,"E88.top")])]})]});}
            var Q5;
            Q5=makeQuery(id+"F6.opExtrude","CAP_EDGE",EDGE,{"disambiguationData":[OSD([sQuery(id+"F0.wireOp",EDGE,"E3")])],"isStart":false});
            chamfer(context, id + "F14", {"entities" : qUnion([Q0, Q1, Q2, Q3, Q4, Q5]), "width" : 1 * mm, "tangentPropagation" : true});
        }
        {
            var Q0;
            Q0=makeQuery(id+"F12.boolean.opBoolean","SPLIT",BODY,{"disambiguationData":[OD(0.0)],"derivedFrom":makeQuery(id+"F1.opExtrude","SWEPT_BODY",BODY,{"disambiguationData":[OSD([sQuery(id+"F0.wireOp",EDGE,"E1.bottom"),sQuery(id+"F0.wireOp",EDGE,"E1.top"),sQuery(id+"F0.wireOp",EDGE,"E2"),sQuery(id+"F0.wireOp",EDGE,"E3"),sQuery(id+"F0.wireOp",EDGE,"E4"),sQuery(id+"F0.wireOp",EDGE,"E5"),sQuery(id+"F0.wireOp",EDGE,"E6"),sQuery(id+"F0.wireOp",EDGE,"E7"),sQuery(id+"F0.wireOp",EDGE,"E8.left"),sQuery(id+"F0.wireOp",EDGE,"E8.right"),sQuery(id+"F0.wireOp",EDGE,"E10.left"),sQuery(id+"F0.wireOp",EDGE,"E12.bottom"),sQuery(id+"F0.wireOp",EDGE,"E12.left"),sQuery(id+"F0.wireOp",EDGE,"E13"),sQuery(id+"F0.wireOp",EDGE,"E14"),sQuery(id+"F0.wireOp",EDGE,"E17.left"),sQuery(id+"F0.wireOp",EDGE,"E17.right"),sQuery(id+"F0.wireOp",EDGE,"E18.left"),sQuery(id+"F0.wireOp",EDGE,"E18.right"),sQuery(id+"F0.wireOp",EDGE,"E19.top"),sQuery(id+"F0.wireOp",EDGE,"E20.bottom"),sQuery(id+"F0.wireOp",EDGE,"E20.left"),sQuery(id+"F0.wireOp",EDGE,"E21.left"),sQuery(id+"F0.wireOp",EDGE,"E22.bottom"),sQuery(id+"F0.wireOp",EDGE,"E22.top"),sQuery(id+"F0.wireOp",EDGE,"E25"),sQuery(id+"F0.wireOp",EDGE,"E26"),sQuery(id+"F0.wireOp",EDGE,"E27"),sQuery(id+"F0.wireOp",EDGE,"E28"),sQuery(id+"F0.wireOp",EDGE,"E30"),sQuery(id+"F0.wireOp",EDGE,"E31"),sQuery(id+"F0.wireOp",EDGE,"E32"),sQuery(id+"F0.wireOp",EDGE,"E33"),sQuery(id+"F0.wireOp",EDGE,"E34.bottom"),sQuery(id+"F0.wireOp",EDGE,"E34.top"),sQuery(id+"F0.wireOp",EDGE,"E35"),sQuery(id+"F0.wireOp",EDGE,"E36"),sQuery(id+"F0.wireOp",EDGE,"E38"),sQuery(id+"F0.wireOp",EDGE,"E40.trimOffspring"),sQuery(id+"F0.wireOp",EDGE,"E41"),sQuery(id+"F0.wireOp",EDGE,"E42"),sQuery(id+"F0.wireOp",EDGE,"E43"),sQuery(id+"F0.wireOp",EDGE,"E44"),sQuery(id+"F0.wireOp",EDGE,"E45"),sQuery(id+"F0.wireOp",EDGE,"E46"),sQuery(id+"F0.wireOp",EDGE,"E47"),sQuery(id+"F0.wireOp",EDGE,"E48.trimOffspring"),sQuery(id+"F0.wireOp",EDGE,"E50.trimOffspring"),sQuery(id+"F0.wireOp",EDGE,"E52"),sQuery(id+"F0.wireOp",EDGE,"E54"),sQuery(id+"F0.wireOp",EDGE,"E55.trimOffspring"),sQuery(id+"F0.wireOp",EDGE,"E56"),sQuery(id+"F0.wireOp",EDGE,"E57"),sQuery(id+"F0.wireOp",EDGE,"E58"),sQuery(id+"F0.wireOp",EDGE,"E59"),sQuery(id+"F0.wireOp",EDGE,"E60"),sQuery(id+"F0.wireOp",EDGE,"E61.trimOffspring"),sQuery(id+"F0.wireOp",EDGE,"E62"),sQuery(id+"F0.wireOp",EDGE,"E63"),sQuery(id+"F0.wireOp",EDGE,"E65"),sQuery(id+"F0.wireOp",EDGE,"E66"),sQuery(id+"F0.wireOp",EDGE,"E67.trimOffspring"),sQuery(id+"F0.wireOp",EDGE,"E68"),sQuery(id+"F0.wireOp",EDGE,"E69"),sQuery(id+"F0.wireOp",EDGE,"E70"),sQuery(id+"F0.wireOp",EDGE,"E71"),sQuery(id+"F0.wireOp",EDGE,"E72"),sQuery(id+"F0.wireOp",EDGE,"E73"),sQuery(id+"F0.wireOp",EDGE,"E74.trimOffspring"),sQuery(id+"F0.wireOp",EDGE,"E75"),sQuery(id+"F0.wireOp",EDGE,"E76"),sQuery(id+"F0.wireOp",EDGE,"E77"),sQuery(id+"F0.wireOp",EDGE,"E78"),sQuery(id+"F0.wireOp",EDGE,"E81.trimOffspring"),sQuery(id+"F0.wireOp",EDGE,"E83.trimOffspring"),sQuery(id+"F0.wireOp",EDGE,"E84.trimOffspring"),sQuery(id+"F0.wireOp",EDGE,"E86")])]})});
            transform(context, id + "F15", {"entities" : qUnion([Q0]), "transformType" : TransformType.TRANSLATION_3D, "dx" : 0 * mm, "dy" : 0 * mm, "dz" : 0 * mm, "makeCopy" : true});
        }
    });
